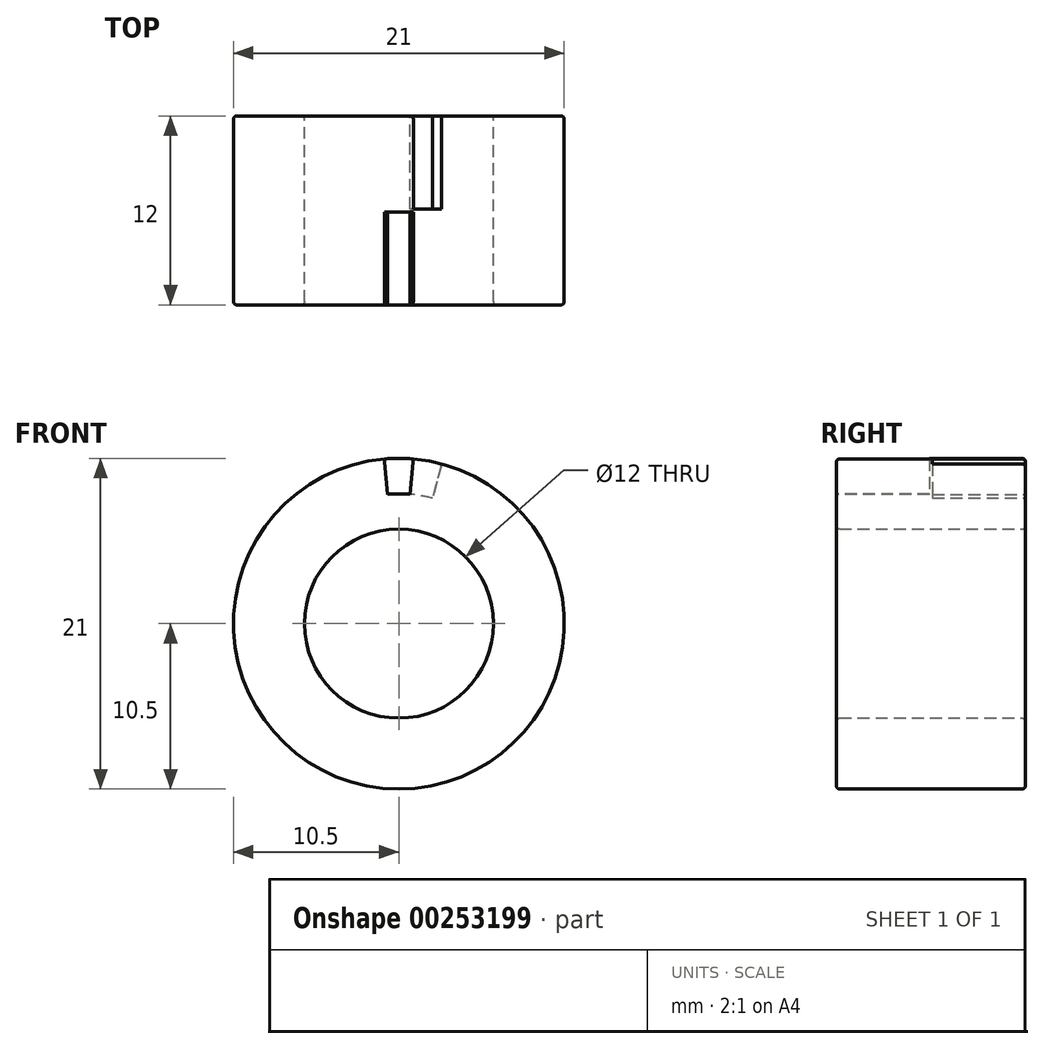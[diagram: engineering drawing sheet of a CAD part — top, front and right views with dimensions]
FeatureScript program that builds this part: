
annotation { "Feature Type Name" : "Feature", "Feature Type Description" : "" }
export const myFeature = defineFeature(function(context is Context, id is Id, definition is map)
    precondition{}
    {
        {
            var Q0;
            Q0=qCreatedBy(makeId("Front.planeOp"),FACE);
            var sketch = newSketch(context, id + "F0", { "sketchPlane" : qUnion([Q0])});
            skCircle(sketch, "E0", {"center": v(0, 0) * mm, "radius": 10.5 * mm});
            skCircle(sketch, "E1", {"center": v(0, 0) * mm, "radius": 6 * mm});
            skSolve(sketch);
        }
        {
            var Q0;
            Q0 = qSketchRegion(id + "F0", true);
            extrude(context, id + "F1", {"entities" : qUnion([Q0]), "depth" : 12 * mm});
        }
        {
            var Q0;
            Q0=makeQuery(id+"F1.opExtrude","CAP_FACE",FACE,{"disambiguationData":[OSD([sQuery(id+"F0.wireOp",EDGE,"E0"),sQuery(id+"F0.wireOp",EDGE,"E1")])],"isStart":false});
            var sketch = newSketch(context, id + "F2", { "sketchPlane" : qUnion([Q0])});
            skLineSegment(sketch, "E2", {"start": v(-0.92, 10.46) * mm, "end": v(-0.72, 8.22) * mm});
            skLineSegment(sketch, "E3", {"start": v(0.92, 10.46) * mm, "end": v(0.72, 8.22) * mm});
            skLineSegment(sketch, "E4", {"start": v(-0.92, 10.46) * mm, "end": v(-0.52, 5.98) * mm, "construction": true});
            skLineSegment(sketch, "E5", {"start": v(-0.52, 5.98) * mm, "end": v(0, 0) * mm, "construction": true});
            skLineSegment(sketch, "E6", {"start": v(0, 0) * mm, "end": v(0.52, 5.98) * mm, "construction": true});
            skLineSegment(sketch, "E7", {"start": v(0.52, 5.98) * mm, "end": v(0.92, 10.46) * mm, "construction": true});
            skPoint(sketch, "E8", {"position": v(-0.72, 8.22) * mm});
            skPoint(sketch, "E9", {"position": v(0.72, 8.22) * mm});
            skArc(sketch, "E10", {"start": v(0.72, 8.22) * mm, "mid": v(0, 8.25) * mm, "end": v(-0.72, 8.22) * mm});
            skArc(sketch, "E11.0", {"start": v(0.92, 10.46) * mm, "mid": v(0, 10.5) * mm, "end": v(-0.92, 10.46) * mm});
            skLineSegment(sketch, "E12", {"start": v(0, 0) * mm, "end": v(0, 8.25) * mm});
            skSolve(sketch);
        }
        {
            var Q0;
            Q0 = qSketchRegion(id + "F2", true);
            extrude(context, id + "F3", {"entities" : qUnion([Q0]), "operationType" : NewBodyOperationType.REMOVE, "oppositeDirection" : true, "depth" : 5.9 * mm});
        }
        {
            var Q0;
            Q0=makeQuery(id+"F1.opExtrude","CAP_FACE",FACE,{"disambiguationData":[OSD([sQuery(id+"F0.wireOp",EDGE,"E0"),sQuery(id+"F0.wireOp",EDGE,"E1")])],"isStart":true});
            var sketch = newSketch(context, id + "F4", { "sketchPlane" : qUnion([Q0])});
            skLineSegment(sketch, "E13", {"start": v(-2.72, 10.14) * mm, "end": v(-2.14, 7.97) * mm});
            skLineSegment(sketch, "E14", {"start": v(-0.92, 10.46) * mm, "end": v(-0.72, 8.22) * mm});
            skLineSegment(sketch, "E15", {"start": v(-2.72, 10.14) * mm, "end": v(-1.55, 5.8) * mm, "construction": true});
            skLineSegment(sketch, "E16", {"start": v(-1.55, 5.8) * mm, "end": v(0, 0) * mm, "construction": true});
            skLineSegment(sketch, "E17", {"start": v(0, 0) * mm, "end": v(-0.52, 5.98) * mm, "construction": true});
            skLineSegment(sketch, "E18", {"start": v(-0.52, 5.98) * mm, "end": v(-0.92, 10.46) * mm, "construction": true});
            skPoint(sketch, "E19", {"position": v(-2.14, 7.97) * mm});
            skPoint(sketch, "E20", {"position": v(-0.72, 8.22) * mm});
            skArc(sketch, "E21", {"start": v(-0.72, 8.22) * mm, "mid": v(-1.43, 8.12) * mm, "end": v(-2.14, 7.97) * mm});
            skArc(sketch, "E22.0", {"start": v(-0.92, 10.46) * mm, "mid": v(-1.82, 10.34) * mm, "end": v(-2.72, 10.14) * mm});
            skLineSegment(sketch, "E23", {"start": v(0, 0) * mm, "end": v(-1.43, 8.12) * mm});
            skSolve(sketch);
        }
        {
            var Q0;
            Q0 = qSketchRegion(id + "F4", true);
            extrude(context, id + "F5", {"entities" : qUnion([Q0]), "operationType" : NewBodyOperationType.REMOVE, "oppositeDirection" : true, "depth" : 5.9 * mm});
        }
        {
            var Q0;
            Q0=makeQuery(id+"F1.opExtrude","CAP_EDGE",EDGE,{"disambiguationData":[OSD([sQuery(id+"F0.wireOp",EDGE,"E1")])],"isStart":true});
            var Q1;
            {var subQ0=sQuery(id+"F0.wireOp",EDGE,"E0");var subQ3=sQuery(id+"F4.wireOp",EDGE,"E14");var subQ4=makeQuery(id+"FM8r0xqs9yAwbjn_1.16.F5.opExtrude","SWEPT_FACE",FACE,{"disambiguationData":[OSD([subQ3])]});var subQ5=sQuery(id+"F4.wireOp",EDGE,"E13");var subQ6=makeQuery(id+"F5.boolean.opBoolean","COPY",FACE,{"derivedFrom":makeQuery(id+"F5.opExtrude","SWEPT_FACE",FACE,{"disambiguationData":[OSD([subQ5])]})});Q1=makeQuery(id+"FM8r0xqs9yAwbjn_1.17.F5.boolean.opBoolean","SPLIT",EDGE,{"disambiguationData":[TD([makeQuery(id+"FM8r0xqs9yAwbjn_1.16.F5.boolean.opBoolean","COPY",FACE,{"derivedFrom":subQ4})])],"derivedFrom":makeQuery(id+"FM8r0xqs9yAwbjn_1.16.F5.boolean.opBoolean","SPLIT",EDGE,{"disambiguationData":[TD([subQ6])],"derivedFrom":makeQuery(id+"FM8r0xqs9yAwbjn_1.15.F5.boolean.opBoolean","SPLIT",EDGE,{"disambiguationData":[TD([subQ6])],"derivedFrom":makeQuery(id+"FM8r0xqs9yAwbjn_1.14.F5.boolean.opBoolean","SPLIT",EDGE,{"disambiguationData":[TD([subQ6])],"derivedFrom":makeQuery(id+"FM8r0xqs9yAwbjn_1.13.F5.boolean.opBoolean","SPLIT",EDGE,{"disambiguationData":[TD([subQ6])],"derivedFrom":makeQuery(id+"FM8r0xqs9yAwbjn_1.12.F5.boolean.opBoolean","SPLIT",EDGE,{"disambiguationData":[TD([subQ6])],"derivedFrom":makeQuery(id+"FM8r0xqs9yAwbjn_1.11.F5.boolean.opBoolean","SPLIT",EDGE,{"disambiguationData":[TD([subQ6])],"derivedFrom":makeQuery(id+"FM8r0xqs9yAwbjn_1.10.F5.boolean.opBoolean","SPLIT",EDGE,{"disambiguationData":[TD([subQ6])],"derivedFrom":makeQuery(id+"FM8r0xqs9yAwbjn_1.9.F5.boolean.opBoolean","SPLIT",EDGE,{"disambiguationData":[TD([subQ6])],"derivedFrom":makeQuery(id+"FM8r0xqs9yAwbjn_1.8.F5.boolean.opBoolean","SPLIT",EDGE,{"disambiguationData":[TD([subQ6])],"derivedFrom":makeQuery(id+"FM8r0xqs9yAwbjn_1.7.F5.boolean.opBoolean","SPLIT",EDGE,{"disambiguationData":[TD([subQ6])],"derivedFrom":makeQuery(id+"FM8r0xqs9yAwbjn_1.6.F5.boolean.opBoolean","SPLIT",EDGE,{"disambiguationData":[TD([subQ6])],"derivedFrom":makeQuery(id+"FM8r0xqs9yAwbjn_1.5.F5.boolean.opBoolean","SPLIT",EDGE,{"disambiguationData":[TD([subQ6])],"derivedFrom":makeQuery(id+"FM8r0xqs9yAwbjn_1.4.F5.boolean.opBoolean","SPLIT",EDGE,{"disambiguationData":[TD([subQ6])],"derivedFrom":makeQuery(id+"FM8r0xqs9yAwbjn_1.3.F5.boolean.opBoolean","SPLIT",EDGE,{"disambiguationData":[TD([subQ6])],"derivedFrom":makeQuery(id+"FM8r0xqs9yAwbjn_1.2.F5.boolean.opBoolean","SPLIT",EDGE,{"disambiguationData":[TD([subQ6])],"derivedFrom":makeQuery(id+"FM8r0xqs9yAwbjn_1.1.F5.boolean.opBoolean","SPLIT",EDGE,{"disambiguationData":[TD([subQ6])],"derivedFrom":makeQuery(id+"F1.opExtrude","CAP_EDGE",EDGE,{"disambiguationData":[OSD([subQ0])],"isStart":true})})})})})})})})})})})})})})})})})});}
            var Q2;
            {var subQ0=sQuery(id+"F0.wireOp",EDGE,"E0");var subQ3=sQuery(id+"F4.wireOp",EDGE,"E14");var subQ4=makeQuery(id+"FM8r0xqs9yAwbjn_1.15.F5.opExtrude","SWEPT_FACE",FACE,{"disambiguationData":[OSD([subQ3])]});var subQ5=sQuery(id+"F4.wireOp",EDGE,"E13");var subQ6=makeQuery(id+"F5.boolean.opBoolean","COPY",FACE,{"derivedFrom":makeQuery(id+"F5.opExtrude","SWEPT_FACE",FACE,{"disambiguationData":[OSD([subQ5])]})});Q2=makeQuery(id+"FM8r0xqs9yAwbjn_1.16.F5.boolean.opBoolean","SPLIT",EDGE,{"disambiguationData":[TD([makeQuery(id+"FM8r0xqs9yAwbjn_1.15.F5.boolean.opBoolean","COPY",FACE,{"derivedFrom":subQ4})])],"derivedFrom":makeQuery(id+"FM8r0xqs9yAwbjn_1.15.F5.boolean.opBoolean","SPLIT",EDGE,{"disambiguationData":[TD([subQ6])],"derivedFrom":makeQuery(id+"FM8r0xqs9yAwbjn_1.14.F5.boolean.opBoolean","SPLIT",EDGE,{"disambiguationData":[TD([subQ6])],"derivedFrom":makeQuery(id+"FM8r0xqs9yAwbjn_1.13.F5.boolean.opBoolean","SPLIT",EDGE,{"disambiguationData":[TD([subQ6])],"derivedFrom":makeQuery(id+"FM8r0xqs9yAwbjn_1.12.F5.boolean.opBoolean","SPLIT",EDGE,{"disambiguationData":[TD([subQ6])],"derivedFrom":makeQuery(id+"FM8r0xqs9yAwbjn_1.11.F5.boolean.opBoolean","SPLIT",EDGE,{"disambiguationData":[TD([subQ6])],"derivedFrom":makeQuery(id+"FM8r0xqs9yAwbjn_1.10.F5.boolean.opBoolean","SPLIT",EDGE,{"disambiguationData":[TD([subQ6])],"derivedFrom":makeQuery(id+"FM8r0xqs9yAwbjn_1.9.F5.boolean.opBoolean","SPLIT",EDGE,{"disambiguationData":[TD([subQ6])],"derivedFrom":makeQuery(id+"FM8r0xqs9yAwbjn_1.8.F5.boolean.opBoolean","SPLIT",EDGE,{"disambiguationData":[TD([subQ6])],"derivedFrom":makeQuery(id+"FM8r0xqs9yAwbjn_1.7.F5.boolean.opBoolean","SPLIT",EDGE,{"disambiguationData":[TD([subQ6])],"derivedFrom":makeQuery(id+"FM8r0xqs9yAwbjn_1.6.F5.boolean.opBoolean","SPLIT",EDGE,{"disambiguationData":[TD([subQ6])],"derivedFrom":makeQuery(id+"FM8r0xqs9yAwbjn_1.5.F5.boolean.opBoolean","SPLIT",EDGE,{"disambiguationData":[TD([subQ6])],"derivedFrom":makeQuery(id+"FM8r0xqs9yAwbjn_1.4.F5.boolean.opBoolean","SPLIT",EDGE,{"disambiguationData":[TD([subQ6])],"derivedFrom":makeQuery(id+"FM8r0xqs9yAwbjn_1.3.F5.boolean.opBoolean","SPLIT",EDGE,{"disambiguationData":[TD([subQ6])],"derivedFrom":makeQuery(id+"FM8r0xqs9yAwbjn_1.2.F5.boolean.opBoolean","SPLIT",EDGE,{"disambiguationData":[TD([subQ6])],"derivedFrom":makeQuery(id+"FM8r0xqs9yAwbjn_1.1.F5.boolean.opBoolean","SPLIT",EDGE,{"disambiguationData":[TD([subQ6])],"derivedFrom":makeQuery(id+"F1.opExtrude","CAP_EDGE",EDGE,{"disambiguationData":[OSD([subQ0])],"isStart":true})})})})})})})})})})})})})})})})});}
            var Q3;
            Q3=makeQuery(id+"FM8r0xqs9yAwbjn_1.16.F5.boolean.opBoolean","COPY",EDGE,{"derivedFrom":makeQuery(id+"FM8r0xqs9yAwbjn_1.16.F5.opExtrude","CAP_EDGE",EDGE,{"disambiguationData":[OSD([sQuery(id+"F4.wireOp",EDGE,"E21")])],"isStart":true})});
            var Q4;
            Q4=makeQuery(id+"FM8r0xqs9yAwbjn_1.16.F5.boolean.opBoolean","COPY",EDGE,{"derivedFrom":makeQuery(id+"FM8r0xqs9yAwbjn_1.16.F5.opExtrude","CAP_EDGE",EDGE,{"disambiguationData":[OSD([sQuery(id+"F4.wireOp",EDGE,"E14")])],"isStart":true})});
            var Q5;
            Q5=makeQuery(id+"FM8r0xqs9yAwbjn_1.16.F5.boolean.opBoolean","COPY",EDGE,{"derivedFrom":makeQuery(id+"FM8r0xqs9yAwbjn_1.16.F5.opExtrude","CAP_EDGE",EDGE,{"disambiguationData":[OSD([sQuery(id+"F4.wireOp",EDGE,"E13")])],"isStart":true})});
            var Q6;
            Q6=makeQuery(id+"FM8r0xqs9yAwbjn_1.16.F5.boolean.opBoolean","COPY",EDGE,{"derivedFrom":makeQuery(id+"FM8r0xqs9yAwbjn_1.16.F5.opExtrude","SWEPT_EDGE",EDGE,{"disambiguationData":[OSD([sQuery(id+"F0.wireOp",EDGE,"E0"),sQuery(id+"F4.wireOp",EDGE,"E13"),sQuery(id+"F4.wireOp",EDGE,"E22.0")])]})});
            var Q7;
            Q7=makeQuery(id+"FM8r0xqs9yAwbjn_1.16.F5.boolean.opBoolean","COPY",EDGE,{"derivedFrom":makeQuery(id+"FM8r0xqs9yAwbjn_1.16.F5.opExtrude","SWEPT_EDGE",EDGE,{"disambiguationData":[OSD([sQuery(id+"F0.wireOp",EDGE,"E0"),sQuery(id+"F4.wireOp",EDGE,"E14"),sQuery(id+"F4.wireOp",EDGE,"E22.0")])]})});
            var Q8;
            Q8=makeQuery(id+"FM8r0xqs9yAwbjn_1.17.F5.boolean.opBoolean","COPY",EDGE,{"derivedFrom":makeQuery(id+"FM8r0xqs9yAwbjn_1.17.F5.opExtrude","SWEPT_EDGE",EDGE,{"disambiguationData":[OSD([sQuery(id+"F0.wireOp",EDGE,"E0"),sQuery(id+"F4.wireOp",EDGE,"E13"),sQuery(id+"F4.wireOp",EDGE,"E22.0")])]})});
            var Q9;
            Q9=makeQuery(id+"FM8r0xqs9yAwbjn_1.17.F5.boolean.opBoolean","COPY",EDGE,{"derivedFrom":makeQuery(id+"FM8r0xqs9yAwbjn_1.17.F5.opExtrude","CAP_EDGE",EDGE,{"disambiguationData":[OSD([sQuery(id+"F4.wireOp",EDGE,"E13")])],"isStart":true})});
            var Q10;
            Q10=makeQuery(id+"FM8r0xqs9yAwbjn_1.17.F5.boolean.opBoolean","COPY",EDGE,{"derivedFrom":makeQuery(id+"FM8r0xqs9yAwbjn_1.17.F5.opExtrude","CAP_EDGE",EDGE,{"disambiguationData":[OSD([sQuery(id+"F4.wireOp",EDGE,"E21")])],"isStart":true})});
            var Q11;
            Q11=makeQuery(id+"FM8r0xqs9yAwbjn_1.17.F5.boolean.opBoolean","COPY",EDGE,{"derivedFrom":makeQuery(id+"FM8r0xqs9yAwbjn_1.17.F5.opExtrude","SWEPT_EDGE",EDGE,{"disambiguationData":[OSD([sQuery(id+"F0.wireOp",EDGE,"E0"),sQuery(id+"F4.wireOp",EDGE,"E14"),sQuery(id+"F4.wireOp",EDGE,"E22.0")])]})});
            var Q12;
            Q12=makeQuery(id+"FM8r0xqs9yAwbjn_1.17.F5.boolean.opBoolean","COPY",EDGE,{"derivedFrom":makeQuery(id+"FM8r0xqs9yAwbjn_1.17.F5.opExtrude","CAP_EDGE",EDGE,{"disambiguationData":[OSD([sQuery(id+"F4.wireOp",EDGE,"E14")])],"isStart":true})});
            var Q13;
            Q13=makeQuery(id+"F5.boolean.opBoolean","COPY",EDGE,{"derivedFrom":makeQuery(id+"F5.opExtrude","SWEPT_EDGE",EDGE,{"disambiguationData":[OSD([sQuery(id+"F0.wireOp",EDGE,"E0"),sQuery(id+"F4.wireOp",EDGE,"E13"),sQuery(id+"F4.wireOp",EDGE,"E22.0")])]})});
            var Q14;
            {var subQ0=sQuery(id+"F0.wireOp",EDGE,"E0");var subQ3=makeQuery(id+"F5.boolean.opBoolean","COPY",FACE,{"derivedFrom":makeQuery(id+"F5.opExtrude","SWEPT_FACE",FACE,{"disambiguationData":[OSD([sQuery(id+"F4.wireOp",EDGE,"E13")])]})});Q14=makeQuery(id+"FM8r0xqs9yAwbjn_1.17.F5.boolean.opBoolean","SPLIT",EDGE,{"disambiguationData":[TD([subQ3])],"derivedFrom":makeQuery(id+"FM8r0xqs9yAwbjn_1.16.F5.boolean.opBoolean","SPLIT",EDGE,{"disambiguationData":[TD([subQ3])],"derivedFrom":makeQuery(id+"FM8r0xqs9yAwbjn_1.15.F5.boolean.opBoolean","SPLIT",EDGE,{"disambiguationData":[TD([subQ3])],"derivedFrom":makeQuery(id+"FM8r0xqs9yAwbjn_1.14.F5.boolean.opBoolean","SPLIT",EDGE,{"disambiguationData":[TD([subQ3])],"derivedFrom":makeQuery(id+"FM8r0xqs9yAwbjn_1.13.F5.boolean.opBoolean","SPLIT",EDGE,{"disambiguationData":[TD([subQ3])],"derivedFrom":makeQuery(id+"FM8r0xqs9yAwbjn_1.12.F5.boolean.opBoolean","SPLIT",EDGE,{"disambiguationData":[TD([subQ3])],"derivedFrom":makeQuery(id+"FM8r0xqs9yAwbjn_1.11.F5.boolean.opBoolean","SPLIT",EDGE,{"disambiguationData":[TD([subQ3])],"derivedFrom":makeQuery(id+"FM8r0xqs9yAwbjn_1.10.F5.boolean.opBoolean","SPLIT",EDGE,{"disambiguationData":[TD([subQ3])],"derivedFrom":makeQuery(id+"FM8r0xqs9yAwbjn_1.9.F5.boolean.opBoolean","SPLIT",EDGE,{"disambiguationData":[TD([subQ3])],"derivedFrom":makeQuery(id+"FM8r0xqs9yAwbjn_1.8.F5.boolean.opBoolean","SPLIT",EDGE,{"disambiguationData":[TD([subQ3])],"derivedFrom":makeQuery(id+"FM8r0xqs9yAwbjn_1.7.F5.boolean.opBoolean","SPLIT",EDGE,{"disambiguationData":[TD([subQ3])],"derivedFrom":makeQuery(id+"FM8r0xqs9yAwbjn_1.6.F5.boolean.opBoolean","SPLIT",EDGE,{"disambiguationData":[TD([subQ3])],"derivedFrom":makeQuery(id+"FM8r0xqs9yAwbjn_1.5.F5.boolean.opBoolean","SPLIT",EDGE,{"disambiguationData":[TD([subQ3])],"derivedFrom":makeQuery(id+"FM8r0xqs9yAwbjn_1.4.F5.boolean.opBoolean","SPLIT",EDGE,{"disambiguationData":[TD([subQ3])],"derivedFrom":makeQuery(id+"FM8r0xqs9yAwbjn_1.3.F5.boolean.opBoolean","SPLIT",EDGE,{"disambiguationData":[TD([subQ3])],"derivedFrom":makeQuery(id+"FM8r0xqs9yAwbjn_1.2.F5.boolean.opBoolean","SPLIT",EDGE,{"disambiguationData":[TD([subQ3])],"derivedFrom":makeQuery(id+"FM8r0xqs9yAwbjn_1.1.F5.boolean.opBoolean","SPLIT",EDGE,{"disambiguationData":[TD([subQ3])],"derivedFrom":makeQuery(id+"F1.opExtrude","CAP_EDGE",EDGE,{"disambiguationData":[OSD([subQ0])],"isStart":true})})})})})})})})})})})})})})})})})});}
            var Q15;
            Q15=makeQuery(id+"F5.boolean.opBoolean","COPY",EDGE,{"derivedFrom":makeQuery(id+"F5.opExtrude","CAP_EDGE",EDGE,{"disambiguationData":[OSD([sQuery(id+"F4.wireOp",EDGE,"E13")])],"isStart":true})});
            var Q16;
            Q16=makeQuery(id+"F5.boolean.opBoolean","COPY",EDGE,{"derivedFrom":makeQuery(id+"F5.opExtrude","CAP_EDGE",EDGE,{"disambiguationData":[OSD([sQuery(id+"F4.wireOp",EDGE,"E21")])],"isStart":true})});
            var Q17;
            Q17=makeQuery(id+"F5.boolean.opBoolean","COPY",EDGE,{"derivedFrom":makeQuery(id+"F5.opExtrude","SWEPT_EDGE",EDGE,{"disambiguationData":[OSD([sQuery(id+"F0.wireOp",EDGE,"E0"),sQuery(id+"F4.wireOp",EDGE,"E14"),sQuery(id+"F4.wireOp",EDGE,"E22.0")])]})});
            var Q18;
            Q18=makeQuery(id+"F5.boolean.opBoolean","COPY",EDGE,{"derivedFrom":makeQuery(id+"F5.opExtrude","CAP_EDGE",EDGE,{"disambiguationData":[OSD([sQuery(id+"F4.wireOp",EDGE,"E14")])],"isStart":true})});
            var Q19;
            Q19=makeQuery(id+"FM8r0xqs9yAwbjn_1.1.F5.boolean.opBoolean","COPY",EDGE,{"derivedFrom":makeQuery(id+"FM8r0xqs9yAwbjn_1.1.F5.opExtrude","CAP_EDGE",EDGE,{"disambiguationData":[OSD([sQuery(id+"F4.wireOp",EDGE,"E13")])],"isStart":true})});
            var Q20;
            Q20=makeQuery(id+"FM8r0xqs9yAwbjn_1.1.F5.boolean.opBoolean","COPY",EDGE,{"derivedFrom":makeQuery(id+"FM8r0xqs9yAwbjn_1.1.F5.opExtrude","SWEPT_EDGE",EDGE,{"disambiguationData":[OSD([sQuery(id+"F0.wireOp",EDGE,"E0"),sQuery(id+"F4.wireOp",EDGE,"E13"),sQuery(id+"F4.wireOp",EDGE,"E22.0")])]})});
            var Q21;
            Q21=makeQuery(id+"FM8r0xqs9yAwbjn_1.1.F5.boolean.opBoolean","COPY",EDGE,{"derivedFrom":makeQuery(id+"FM8r0xqs9yAwbjn_1.1.F5.opExtrude","SWEPT_EDGE",EDGE,{"disambiguationData":[OSD([sQuery(id+"F0.wireOp",EDGE,"E0"),sQuery(id+"F4.wireOp",EDGE,"E14"),sQuery(id+"F4.wireOp",EDGE,"E22.0")])]})});
            var Q22;
            Q22=makeQuery(id+"FM8r0xqs9yAwbjn_1.1.F5.boolean.opBoolean","COPY",EDGE,{"derivedFrom":makeQuery(id+"FM8r0xqs9yAwbjn_1.1.F5.opExtrude","CAP_EDGE",EDGE,{"disambiguationData":[OSD([sQuery(id+"F4.wireOp",EDGE,"E14")])],"isStart":true})});
            var Q23;
            Q23=makeQuery(id+"FM8r0xqs9yAwbjn_1.1.F5.boolean.opBoolean","COPY",EDGE,{"derivedFrom":makeQuery(id+"FM8r0xqs9yAwbjn_1.1.F5.opExtrude","CAP_EDGE",EDGE,{"disambiguationData":[OSD([sQuery(id+"F4.wireOp",EDGE,"E21")])],"isStart":true})});
            var Q24;
            {var subQ0=sQuery(id+"F0.wireOp",EDGE,"E0");var subQ3=makeQuery(id+"FM8r0xqs9yAwbjn_1.1.F5.opExtrude","SWEPT_FACE",FACE,{"disambiguationData":[OSD([sQuery(id+"F4.wireOp",EDGE,"E14")])]});var subQ4=sQuery(id+"F4.wireOp",EDGE,"E13");Q24=makeQuery(id+"FM8r0xqs9yAwbjn_1.2.F5.boolean.opBoolean","SPLIT",EDGE,{"disambiguationData":[TD([makeQuery(id+"FM8r0xqs9yAwbjn_1.1.F5.boolean.opBoolean","COPY",FACE,{"derivedFrom":subQ3})])],"derivedFrom":makeQuery(id+"FM8r0xqs9yAwbjn_1.1.F5.boolean.opBoolean","SPLIT",EDGE,{"disambiguationData":[TD([makeQuery(id+"F5.boolean.opBoolean","COPY",FACE,{"derivedFrom":makeQuery(id+"F5.opExtrude","SWEPT_FACE",FACE,{"disambiguationData":[OSD([subQ4])]})})])],"derivedFrom":makeQuery(id+"F1.opExtrude","CAP_EDGE",EDGE,{"disambiguationData":[OSD([subQ0])],"isStart":true})})});}
            var Q25;
            Q25=makeQuery(id+"FM8r0xqs9yAwbjn_1.2.F5.boolean.opBoolean","COPY",EDGE,{"derivedFrom":makeQuery(id+"FM8r0xqs9yAwbjn_1.2.F5.opExtrude","CAP_EDGE",EDGE,{"disambiguationData":[OSD([sQuery(id+"F4.wireOp",EDGE,"E13")])],"isStart":true})});
            var Q26;
            Q26=makeQuery(id+"FM8r0xqs9yAwbjn_1.2.F5.boolean.opBoolean","COPY",EDGE,{"derivedFrom":makeQuery(id+"FM8r0xqs9yAwbjn_1.2.F5.opExtrude","SWEPT_EDGE",EDGE,{"disambiguationData":[OSD([sQuery(id+"F0.wireOp",EDGE,"E0"),sQuery(id+"F4.wireOp",EDGE,"E13"),sQuery(id+"F4.wireOp",EDGE,"E22.0")])]})});
            var Q27;
            Q27=makeQuery(id+"FM8r0xqs9yAwbjn_1.2.F5.boolean.opBoolean","COPY",EDGE,{"derivedFrom":makeQuery(id+"FM8r0xqs9yAwbjn_1.2.F5.opExtrude","SWEPT_EDGE",EDGE,{"disambiguationData":[OSD([sQuery(id+"F0.wireOp",EDGE,"E0"),sQuery(id+"F4.wireOp",EDGE,"E14"),sQuery(id+"F4.wireOp",EDGE,"E22.0")])]})});
            var Q28;
            Q28=makeQuery(id+"FM8r0xqs9yAwbjn_1.2.F5.boolean.opBoolean","COPY",EDGE,{"derivedFrom":makeQuery(id+"FM8r0xqs9yAwbjn_1.2.F5.opExtrude","CAP_EDGE",EDGE,{"disambiguationData":[OSD([sQuery(id+"F4.wireOp",EDGE,"E21")])],"isStart":true})});
            var Q29;
            Q29=makeQuery(id+"FM8r0xqs9yAwbjn_1.2.F5.boolean.opBoolean","COPY",EDGE,{"derivedFrom":makeQuery(id+"FM8r0xqs9yAwbjn_1.2.F5.opExtrude","CAP_EDGE",EDGE,{"disambiguationData":[OSD([sQuery(id+"F4.wireOp",EDGE,"E14")])],"isStart":true})});
            var Q30;
            {var subQ0=sQuery(id+"F0.wireOp",EDGE,"E0");var subQ3=sQuery(id+"F4.wireOp",EDGE,"E14");var subQ4=makeQuery(id+"FM8r0xqs9yAwbjn_1.2.F5.opExtrude","SWEPT_FACE",FACE,{"disambiguationData":[OSD([subQ3])]});var subQ5=sQuery(id+"F4.wireOp",EDGE,"E13");var subQ6=makeQuery(id+"F5.boolean.opBoolean","COPY",FACE,{"derivedFrom":makeQuery(id+"F5.opExtrude","SWEPT_FACE",FACE,{"disambiguationData":[OSD([subQ5])]})});Q30=makeQuery(id+"FM8r0xqs9yAwbjn_1.3.F5.boolean.opBoolean","SPLIT",EDGE,{"disambiguationData":[TD([makeQuery(id+"FM8r0xqs9yAwbjn_1.2.F5.boolean.opBoolean","COPY",FACE,{"derivedFrom":subQ4})])],"derivedFrom":makeQuery(id+"FM8r0xqs9yAwbjn_1.2.F5.boolean.opBoolean","SPLIT",EDGE,{"disambiguationData":[TD([subQ6])],"derivedFrom":makeQuery(id+"FM8r0xqs9yAwbjn_1.1.F5.boolean.opBoolean","SPLIT",EDGE,{"disambiguationData":[TD([subQ6])],"derivedFrom":makeQuery(id+"F1.opExtrude","CAP_EDGE",EDGE,{"disambiguationData":[OSD([subQ0])],"isStart":true})})})});}
            var Q31;
            Q31=makeQuery(id+"FM8r0xqs9yAwbjn_1.3.F5.boolean.opBoolean","COPY",EDGE,{"derivedFrom":makeQuery(id+"FM8r0xqs9yAwbjn_1.3.F5.opExtrude","CAP_EDGE",EDGE,{"disambiguationData":[OSD([sQuery(id+"F4.wireOp",EDGE,"E13")])],"isStart":true})});
            var Q32;
            Q32=makeQuery(id+"FM8r0xqs9yAwbjn_1.3.F5.boolean.opBoolean","COPY",EDGE,{"derivedFrom":makeQuery(id+"FM8r0xqs9yAwbjn_1.3.F5.opExtrude","SWEPT_EDGE",EDGE,{"disambiguationData":[OSD([sQuery(id+"F0.wireOp",EDGE,"E0"),sQuery(id+"F4.wireOp",EDGE,"E13"),sQuery(id+"F4.wireOp",EDGE,"E22.0")])]})});
            var Q33;
            Q33=makeQuery(id+"FM8r0xqs9yAwbjn_1.3.F5.boolean.opBoolean","COPY",EDGE,{"derivedFrom":makeQuery(id+"FM8r0xqs9yAwbjn_1.3.F5.opExtrude","SWEPT_EDGE",EDGE,{"disambiguationData":[OSD([sQuery(id+"F0.wireOp",EDGE,"E0"),sQuery(id+"F4.wireOp",EDGE,"E14"),sQuery(id+"F4.wireOp",EDGE,"E22.0")])]})});
            var Q34;
            Q34=makeQuery(id+"FM8r0xqs9yAwbjn_1.3.F5.boolean.opBoolean","COPY",EDGE,{"derivedFrom":makeQuery(id+"FM8r0xqs9yAwbjn_1.3.F5.opExtrude","CAP_EDGE",EDGE,{"disambiguationData":[OSD([sQuery(id+"F4.wireOp",EDGE,"E21")])],"isStart":true})});
            var Q35;
            {var subQ0=sQuery(id+"F0.wireOp",EDGE,"E0");var subQ3=sQuery(id+"F4.wireOp",EDGE,"E14");var subQ4=makeQuery(id+"FM8r0xqs9yAwbjn_1.3.F5.opExtrude","SWEPT_FACE",FACE,{"disambiguationData":[OSD([subQ3])]});var subQ5=sQuery(id+"F4.wireOp",EDGE,"E13");var subQ6=makeQuery(id+"F5.boolean.opBoolean","COPY",FACE,{"derivedFrom":makeQuery(id+"F5.opExtrude","SWEPT_FACE",FACE,{"disambiguationData":[OSD([subQ5])]})});Q35=makeQuery(id+"FM8r0xqs9yAwbjn_1.4.F5.boolean.opBoolean","SPLIT",EDGE,{"disambiguationData":[TD([makeQuery(id+"FM8r0xqs9yAwbjn_1.3.F5.boolean.opBoolean","COPY",FACE,{"derivedFrom":subQ4})])],"derivedFrom":makeQuery(id+"FM8r0xqs9yAwbjn_1.3.F5.boolean.opBoolean","SPLIT",EDGE,{"disambiguationData":[TD([subQ6])],"derivedFrom":makeQuery(id+"FM8r0xqs9yAwbjn_1.2.F5.boolean.opBoolean","SPLIT",EDGE,{"disambiguationData":[TD([subQ6])],"derivedFrom":makeQuery(id+"FM8r0xqs9yAwbjn_1.1.F5.boolean.opBoolean","SPLIT",EDGE,{"disambiguationData":[TD([subQ6])],"derivedFrom":makeQuery(id+"F1.opExtrude","CAP_EDGE",EDGE,{"disambiguationData":[OSD([subQ0])],"isStart":true})})})})});}
            var Q36;
            Q36=makeQuery(id+"FM8r0xqs9yAwbjn_1.4.F5.boolean.opBoolean","COPY",EDGE,{"derivedFrom":makeQuery(id+"FM8r0xqs9yAwbjn_1.4.F5.opExtrude","CAP_EDGE",EDGE,{"disambiguationData":[OSD([sQuery(id+"F4.wireOp",EDGE,"E13")])],"isStart":true})});
            var Q37;
            Q37=makeQuery(id+"FM8r0xqs9yAwbjn_1.4.F5.boolean.opBoolean","COPY",EDGE,{"derivedFrom":makeQuery(id+"FM8r0xqs9yAwbjn_1.4.F5.opExtrude","SWEPT_EDGE",EDGE,{"disambiguationData":[OSD([sQuery(id+"F0.wireOp",EDGE,"E0"),sQuery(id+"F4.wireOp",EDGE,"E13"),sQuery(id+"F4.wireOp",EDGE,"E22.0")])]})});
            var Q38;
            Q38=makeQuery(id+"FM8r0xqs9yAwbjn_1.4.F5.boolean.opBoolean","COPY",EDGE,{"derivedFrom":makeQuery(id+"FM8r0xqs9yAwbjn_1.4.F5.opExtrude","SWEPT_EDGE",EDGE,{"disambiguationData":[OSD([sQuery(id+"F0.wireOp",EDGE,"E0"),sQuery(id+"F4.wireOp",EDGE,"E14"),sQuery(id+"F4.wireOp",EDGE,"E22.0")])]})});
            var Q39;
            Q39=makeQuery(id+"FM8r0xqs9yAwbjn_1.4.F5.boolean.opBoolean","COPY",EDGE,{"derivedFrom":makeQuery(id+"FM8r0xqs9yAwbjn_1.4.F5.opExtrude","CAP_EDGE",EDGE,{"disambiguationData":[OSD([sQuery(id+"F4.wireOp",EDGE,"E21")])],"isStart":true})});
            var Q40;
            Q40=makeQuery(id+"FM8r0xqs9yAwbjn_1.4.F5.boolean.opBoolean","COPY",EDGE,{"derivedFrom":makeQuery(id+"FM8r0xqs9yAwbjn_1.4.F5.opExtrude","CAP_EDGE",EDGE,{"disambiguationData":[OSD([sQuery(id+"F4.wireOp",EDGE,"E14")])],"isStart":true})});
            var Q41;
            {var subQ0=sQuery(id+"F0.wireOp",EDGE,"E0");var subQ3=sQuery(id+"F4.wireOp",EDGE,"E14");var subQ4=makeQuery(id+"FM8r0xqs9yAwbjn_1.4.F5.opExtrude","SWEPT_FACE",FACE,{"disambiguationData":[OSD([subQ3])]});var subQ5=sQuery(id+"F4.wireOp",EDGE,"E13");var subQ6=makeQuery(id+"F5.boolean.opBoolean","COPY",FACE,{"derivedFrom":makeQuery(id+"F5.opExtrude","SWEPT_FACE",FACE,{"disambiguationData":[OSD([subQ5])]})});Q41=makeQuery(id+"FM8r0xqs9yAwbjn_1.5.F5.boolean.opBoolean","SPLIT",EDGE,{"disambiguationData":[TD([makeQuery(id+"FM8r0xqs9yAwbjn_1.4.F5.boolean.opBoolean","COPY",FACE,{"derivedFrom":subQ4})])],"derivedFrom":makeQuery(id+"FM8r0xqs9yAwbjn_1.4.F5.boolean.opBoolean","SPLIT",EDGE,{"disambiguationData":[TD([subQ6])],"derivedFrom":makeQuery(id+"FM8r0xqs9yAwbjn_1.3.F5.boolean.opBoolean","SPLIT",EDGE,{"disambiguationData":[TD([subQ6])],"derivedFrom":makeQuery(id+"FM8r0xqs9yAwbjn_1.2.F5.boolean.opBoolean","SPLIT",EDGE,{"disambiguationData":[TD([subQ6])],"derivedFrom":makeQuery(id+"FM8r0xqs9yAwbjn_1.1.F5.boolean.opBoolean","SPLIT",EDGE,{"disambiguationData":[TD([subQ6])],"derivedFrom":makeQuery(id+"F1.opExtrude","CAP_EDGE",EDGE,{"disambiguationData":[OSD([subQ0])],"isStart":true})})})})})});}
            var Q42;
            Q42=makeQuery(id+"FM8r0xqs9yAwbjn_1.5.F5.boolean.opBoolean","COPY",EDGE,{"derivedFrom":makeQuery(id+"FM8r0xqs9yAwbjn_1.5.F5.opExtrude","CAP_EDGE",EDGE,{"disambiguationData":[OSD([sQuery(id+"F4.wireOp",EDGE,"E13")])],"isStart":true})});
            var Q43;
            Q43=makeQuery(id+"FM8r0xqs9yAwbjn_1.5.F5.boolean.opBoolean","COPY",EDGE,{"derivedFrom":makeQuery(id+"FM8r0xqs9yAwbjn_1.5.F5.opExtrude","CAP_EDGE",EDGE,{"disambiguationData":[OSD([sQuery(id+"F4.wireOp",EDGE,"E21")])],"isStart":true})});
            var Q44;
            Q44=makeQuery(id+"FM8r0xqs9yAwbjn_1.5.F5.boolean.opBoolean","COPY",EDGE,{"derivedFrom":makeQuery(id+"FM8r0xqs9yAwbjn_1.5.F5.opExtrude","CAP_EDGE",EDGE,{"disambiguationData":[OSD([sQuery(id+"F4.wireOp",EDGE,"E14")])],"isStart":true})});
            var Q45;
            Q45=makeQuery(id+"FM8r0xqs9yAwbjn_1.5.F5.boolean.opBoolean","COPY",EDGE,{"derivedFrom":makeQuery(id+"FM8r0xqs9yAwbjn_1.5.F5.opExtrude","SWEPT_EDGE",EDGE,{"disambiguationData":[OSD([sQuery(id+"F0.wireOp",EDGE,"E0"),sQuery(id+"F4.wireOp",EDGE,"E13"),sQuery(id+"F4.wireOp",EDGE,"E22.0")])]})});
            var Q46;
            Q46=makeQuery(id+"FM8r0xqs9yAwbjn_1.5.F5.boolean.opBoolean","COPY",EDGE,{"derivedFrom":makeQuery(id+"FM8r0xqs9yAwbjn_1.5.F5.opExtrude","SWEPT_EDGE",EDGE,{"disambiguationData":[OSD([sQuery(id+"F0.wireOp",EDGE,"E0"),sQuery(id+"F4.wireOp",EDGE,"E14"),sQuery(id+"F4.wireOp",EDGE,"E22.0")])]})});
            var Q47;
            Q47=makeQuery(id+"FM8r0xqs9yAwbjn_1.6.F5.boolean.opBoolean","COPY",EDGE,{"derivedFrom":makeQuery(id+"FM8r0xqs9yAwbjn_1.6.F5.opExtrude","SWEPT_EDGE",EDGE,{"disambiguationData":[OSD([sQuery(id+"F0.wireOp",EDGE,"E0"),sQuery(id+"F4.wireOp",EDGE,"E13"),sQuery(id+"F4.wireOp",EDGE,"E22.0")])]})});
            var Q48;
            Q48=makeQuery(id+"FM8r0xqs9yAwbjn_1.6.F5.boolean.opBoolean","COPY",EDGE,{"derivedFrom":makeQuery(id+"FM8r0xqs9yAwbjn_1.6.F5.opExtrude","SWEPT_EDGE",EDGE,{"disambiguationData":[OSD([sQuery(id+"F0.wireOp",EDGE,"E0"),sQuery(id+"F4.wireOp",EDGE,"E14"),sQuery(id+"F4.wireOp",EDGE,"E22.0")])]})});
            var Q49;
            Q49=makeQuery(id+"FM8r0xqs9yAwbjn_1.6.F5.boolean.opBoolean","COPY",EDGE,{"derivedFrom":makeQuery(id+"FM8r0xqs9yAwbjn_1.6.F5.opExtrude","CAP_EDGE",EDGE,{"disambiguationData":[OSD([sQuery(id+"F4.wireOp",EDGE,"E13")])],"isStart":true})});
            var Q50;
            {var subQ0=sQuery(id+"F0.wireOp",EDGE,"E0");var subQ3=sQuery(id+"F4.wireOp",EDGE,"E14");var subQ4=makeQuery(id+"FM8r0xqs9yAwbjn_1.5.F5.opExtrude","SWEPT_FACE",FACE,{"disambiguationData":[OSD([subQ3])]});var subQ5=sQuery(id+"F4.wireOp",EDGE,"E13");var subQ6=makeQuery(id+"F5.boolean.opBoolean","COPY",FACE,{"derivedFrom":makeQuery(id+"F5.opExtrude","SWEPT_FACE",FACE,{"disambiguationData":[OSD([subQ5])]})});Q50=makeQuery(id+"FM8r0xqs9yAwbjn_1.6.F5.boolean.opBoolean","SPLIT",EDGE,{"disambiguationData":[TD([makeQuery(id+"FM8r0xqs9yAwbjn_1.5.F5.boolean.opBoolean","COPY",FACE,{"derivedFrom":subQ4})])],"derivedFrom":makeQuery(id+"FM8r0xqs9yAwbjn_1.5.F5.boolean.opBoolean","SPLIT",EDGE,{"disambiguationData":[TD([subQ6])],"derivedFrom":makeQuery(id+"FM8r0xqs9yAwbjn_1.4.F5.boolean.opBoolean","SPLIT",EDGE,{"disambiguationData":[TD([subQ6])],"derivedFrom":makeQuery(id+"FM8r0xqs9yAwbjn_1.3.F5.boolean.opBoolean","SPLIT",EDGE,{"disambiguationData":[TD([subQ6])],"derivedFrom":makeQuery(id+"FM8r0xqs9yAwbjn_1.2.F5.boolean.opBoolean","SPLIT",EDGE,{"disambiguationData":[TD([subQ6])],"derivedFrom":makeQuery(id+"FM8r0xqs9yAwbjn_1.1.F5.boolean.opBoolean","SPLIT",EDGE,{"disambiguationData":[TD([subQ6])],"derivedFrom":makeQuery(id+"F1.opExtrude","CAP_EDGE",EDGE,{"disambiguationData":[OSD([subQ0])],"isStart":true})})})})})})});}
            var Q51;
            Q51=makeQuery(id+"FM8r0xqs9yAwbjn_1.6.F5.boolean.opBoolean","COPY",EDGE,{"derivedFrom":makeQuery(id+"FM8r0xqs9yAwbjn_1.6.F5.opExtrude","CAP_EDGE",EDGE,{"disambiguationData":[OSD([sQuery(id+"F4.wireOp",EDGE,"E21")])],"isStart":true})});
            var Q52;
            Q52=makeQuery(id+"FM8r0xqs9yAwbjn_1.6.F5.boolean.opBoolean","COPY",EDGE,{"derivedFrom":makeQuery(id+"FM8r0xqs9yAwbjn_1.6.F5.opExtrude","CAP_EDGE",EDGE,{"disambiguationData":[OSD([sQuery(id+"F4.wireOp",EDGE,"E14")])],"isStart":true})});
            var Q53;
            Q53=makeQuery(id+"FM8r0xqs9yAwbjn_1.7.F5.boolean.opBoolean","COPY",EDGE,{"derivedFrom":makeQuery(id+"FM8r0xqs9yAwbjn_1.7.F5.opExtrude","CAP_EDGE",EDGE,{"disambiguationData":[OSD([sQuery(id+"F4.wireOp",EDGE,"E13")])],"isStart":true})});
            var Q54;
            Q54=makeQuery(id+"FM8r0xqs9yAwbjn_1.7.F5.boolean.opBoolean","COPY",EDGE,{"derivedFrom":makeQuery(id+"FM8r0xqs9yAwbjn_1.7.F5.opExtrude","CAP_EDGE",EDGE,{"disambiguationData":[OSD([sQuery(id+"F4.wireOp",EDGE,"E21")])],"isStart":true})});
            var Q55;
            Q55=makeQuery(id+"FM8r0xqs9yAwbjn_1.7.F5.boolean.opBoolean","COPY",EDGE,{"derivedFrom":makeQuery(id+"FM8r0xqs9yAwbjn_1.7.F5.opExtrude","CAP_EDGE",EDGE,{"disambiguationData":[OSD([sQuery(id+"F4.wireOp",EDGE,"E14")])],"isStart":true})});
            var Q56;
            Q56=makeQuery(id+"FM8r0xqs9yAwbjn_1.7.F5.boolean.opBoolean","COPY",EDGE,{"derivedFrom":makeQuery(id+"FM8r0xqs9yAwbjn_1.7.F5.opExtrude","SWEPT_EDGE",EDGE,{"disambiguationData":[OSD([sQuery(id+"F0.wireOp",EDGE,"E0"),sQuery(id+"F4.wireOp",EDGE,"E14"),sQuery(id+"F4.wireOp",EDGE,"E22.0")])]})});
            var Q57;
            Q57=makeQuery(id+"FM8r0xqs9yAwbjn_1.7.F5.boolean.opBoolean","COPY",EDGE,{"derivedFrom":makeQuery(id+"FM8r0xqs9yAwbjn_1.7.F5.opExtrude","SWEPT_EDGE",EDGE,{"disambiguationData":[OSD([sQuery(id+"F0.wireOp",EDGE,"E0"),sQuery(id+"F4.wireOp",EDGE,"E13"),sQuery(id+"F4.wireOp",EDGE,"E22.0")])]})});
            var Q58;
            Q58=makeQuery(id+"FM8r0xqs9yAwbjn_1.8.F5.boolean.opBoolean","COPY",EDGE,{"derivedFrom":makeQuery(id+"FM8r0xqs9yAwbjn_1.8.F5.opExtrude","CAP_EDGE",EDGE,{"disambiguationData":[OSD([sQuery(id+"F4.wireOp",EDGE,"E13")])],"isStart":true})});
            var Q59;
            Q59=makeQuery(id+"FM8r0xqs9yAwbjn_1.8.F5.boolean.opBoolean","COPY",EDGE,{"derivedFrom":makeQuery(id+"FM8r0xqs9yAwbjn_1.8.F5.opExtrude","CAP_EDGE",EDGE,{"disambiguationData":[OSD([sQuery(id+"F4.wireOp",EDGE,"E21")])],"isStart":true})});
            var Q60;
            Q60=makeQuery(id+"FM8r0xqs9yAwbjn_1.8.F5.boolean.opBoolean","COPY",EDGE,{"derivedFrom":makeQuery(id+"FM8r0xqs9yAwbjn_1.8.F5.opExtrude","CAP_EDGE",EDGE,{"disambiguationData":[OSD([sQuery(id+"F4.wireOp",EDGE,"E14")])],"isStart":true})});
            var Q61;
            Q61=makeQuery(id+"FM8r0xqs9yAwbjn_1.8.F5.boolean.opBoolean","COPY",EDGE,{"derivedFrom":makeQuery(id+"FM8r0xqs9yAwbjn_1.8.F5.opExtrude","SWEPT_EDGE",EDGE,{"disambiguationData":[OSD([sQuery(id+"F0.wireOp",EDGE,"E0"),sQuery(id+"F4.wireOp",EDGE,"E14"),sQuery(id+"F4.wireOp",EDGE,"E22.0")])]})});
            var Q62;
            Q62=makeQuery(id+"FM8r0xqs9yAwbjn_1.8.F5.boolean.opBoolean","COPY",EDGE,{"derivedFrom":makeQuery(id+"FM8r0xqs9yAwbjn_1.8.F5.opExtrude","SWEPT_EDGE",EDGE,{"disambiguationData":[OSD([sQuery(id+"F0.wireOp",EDGE,"E0"),sQuery(id+"F4.wireOp",EDGE,"E13"),sQuery(id+"F4.wireOp",EDGE,"E22.0")])]})});
            var Q63;
            {var subQ0=sQuery(id+"F0.wireOp",EDGE,"E0");var subQ3=sQuery(id+"F4.wireOp",EDGE,"E13");var subQ4=sQuery(id+"F4.wireOp",EDGE,"E14");var subQ5=makeQuery(id+"FM8r0xqs9yAwbjn_1.7.F5.opExtrude","SWEPT_FACE",FACE,{"disambiguationData":[OSD([subQ4])]});var subQ6=makeQuery(id+"F5.boolean.opBoolean","COPY",FACE,{"derivedFrom":makeQuery(id+"F5.opExtrude","SWEPT_FACE",FACE,{"disambiguationData":[OSD([subQ3])]})});Q63=makeQuery(id+"FM8r0xqs9yAwbjn_1.8.F5.boolean.opBoolean","SPLIT",EDGE,{"disambiguationData":[TD([makeQuery(id+"FM8r0xqs9yAwbjn_1.7.F5.boolean.opBoolean","COPY",FACE,{"derivedFrom":subQ5})])],"derivedFrom":makeQuery(id+"FM8r0xqs9yAwbjn_1.7.F5.boolean.opBoolean","SPLIT",EDGE,{"disambiguationData":[TD([subQ6])],"derivedFrom":makeQuery(id+"FM8r0xqs9yAwbjn_1.6.F5.boolean.opBoolean","SPLIT",EDGE,{"disambiguationData":[TD([subQ6])],"derivedFrom":makeQuery(id+"FM8r0xqs9yAwbjn_1.5.F5.boolean.opBoolean","SPLIT",EDGE,{"disambiguationData":[TD([subQ6])],"derivedFrom":makeQuery(id+"FM8r0xqs9yAwbjn_1.4.F5.boolean.opBoolean","SPLIT",EDGE,{"disambiguationData":[TD([subQ6])],"derivedFrom":makeQuery(id+"FM8r0xqs9yAwbjn_1.3.F5.boolean.opBoolean","SPLIT",EDGE,{"disambiguationData":[TD([subQ6])],"derivedFrom":makeQuery(id+"FM8r0xqs9yAwbjn_1.2.F5.boolean.opBoolean","SPLIT",EDGE,{"disambiguationData":[TD([subQ6])],"derivedFrom":makeQuery(id+"FM8r0xqs9yAwbjn_1.1.F5.boolean.opBoolean","SPLIT",EDGE,{"disambiguationData":[TD([subQ6])],"derivedFrom":makeQuery(id+"F1.opExtrude","CAP_EDGE",EDGE,{"disambiguationData":[OSD([subQ0])],"isStart":true})})})})})})})})});}
            var Q64;
            {var subQ0=sQuery(id+"F0.wireOp",EDGE,"E0");var subQ3=sQuery(id+"F4.wireOp",EDGE,"E14");var subQ4=makeQuery(id+"FM8r0xqs9yAwbjn_1.6.F5.opExtrude","SWEPT_FACE",FACE,{"disambiguationData":[OSD([subQ3])]});var subQ5=sQuery(id+"F4.wireOp",EDGE,"E13");var subQ6=makeQuery(id+"F5.boolean.opBoolean","COPY",FACE,{"derivedFrom":makeQuery(id+"F5.opExtrude","SWEPT_FACE",FACE,{"disambiguationData":[OSD([subQ5])]})});Q64=makeQuery(id+"FM8r0xqs9yAwbjn_1.7.F5.boolean.opBoolean","SPLIT",EDGE,{"disambiguationData":[TD([makeQuery(id+"FM8r0xqs9yAwbjn_1.6.F5.boolean.opBoolean","COPY",FACE,{"derivedFrom":subQ4})])],"derivedFrom":makeQuery(id+"FM8r0xqs9yAwbjn_1.6.F5.boolean.opBoolean","SPLIT",EDGE,{"disambiguationData":[TD([subQ6])],"derivedFrom":makeQuery(id+"FM8r0xqs9yAwbjn_1.5.F5.boolean.opBoolean","SPLIT",EDGE,{"disambiguationData":[TD([subQ6])],"derivedFrom":makeQuery(id+"FM8r0xqs9yAwbjn_1.4.F5.boolean.opBoolean","SPLIT",EDGE,{"disambiguationData":[TD([subQ6])],"derivedFrom":makeQuery(id+"FM8r0xqs9yAwbjn_1.3.F5.boolean.opBoolean","SPLIT",EDGE,{"disambiguationData":[TD([subQ6])],"derivedFrom":makeQuery(id+"FM8r0xqs9yAwbjn_1.2.F5.boolean.opBoolean","SPLIT",EDGE,{"disambiguationData":[TD([subQ6])],"derivedFrom":makeQuery(id+"FM8r0xqs9yAwbjn_1.1.F5.boolean.opBoolean","SPLIT",EDGE,{"disambiguationData":[TD([subQ6])],"derivedFrom":makeQuery(id+"F1.opExtrude","CAP_EDGE",EDGE,{"disambiguationData":[OSD([subQ0])],"isStart":true})})})})})})})});}
            var Q65;
            Q65=makeQuery(id+"FM8r0xqs9yAwbjn_1.9.F5.boolean.opBoolean","COPY",EDGE,{"derivedFrom":makeQuery(id+"FM8r0xqs9yAwbjn_1.9.F5.opExtrude","CAP_EDGE",EDGE,{"disambiguationData":[OSD([sQuery(id+"F4.wireOp",EDGE,"E21")])],"isStart":true})});
            var Q66;
            Q66=makeQuery(id+"FM8r0xqs9yAwbjn_1.9.F5.boolean.opBoolean","COPY",EDGE,{"derivedFrom":makeQuery(id+"FM8r0xqs9yAwbjn_1.9.F5.opExtrude","CAP_EDGE",EDGE,{"disambiguationData":[OSD([sQuery(id+"F4.wireOp",EDGE,"E13")])],"isStart":true})});
            var Q67;
            {var subQ0=sQuery(id+"F0.wireOp",EDGE,"E0");var subQ3=sQuery(id+"F4.wireOp",EDGE,"E13");var subQ4=sQuery(id+"F4.wireOp",EDGE,"E14");var subQ5=makeQuery(id+"FM8r0xqs9yAwbjn_1.8.F5.opExtrude","SWEPT_FACE",FACE,{"disambiguationData":[OSD([subQ4])]});var subQ6=makeQuery(id+"F5.boolean.opBoolean","COPY",FACE,{"derivedFrom":makeQuery(id+"F5.opExtrude","SWEPT_FACE",FACE,{"disambiguationData":[OSD([subQ3])]})});Q67=makeQuery(id+"FM8r0xqs9yAwbjn_1.9.F5.boolean.opBoolean","SPLIT",EDGE,{"disambiguationData":[TD([makeQuery(id+"FM8r0xqs9yAwbjn_1.8.F5.boolean.opBoolean","COPY",FACE,{"derivedFrom":subQ5})])],"derivedFrom":makeQuery(id+"FM8r0xqs9yAwbjn_1.8.F5.boolean.opBoolean","SPLIT",EDGE,{"disambiguationData":[TD([subQ6])],"derivedFrom":makeQuery(id+"FM8r0xqs9yAwbjn_1.7.F5.boolean.opBoolean","SPLIT",EDGE,{"disambiguationData":[TD([subQ6])],"derivedFrom":makeQuery(id+"FM8r0xqs9yAwbjn_1.6.F5.boolean.opBoolean","SPLIT",EDGE,{"disambiguationData":[TD([subQ6])],"derivedFrom":makeQuery(id+"FM8r0xqs9yAwbjn_1.5.F5.boolean.opBoolean","SPLIT",EDGE,{"disambiguationData":[TD([subQ6])],"derivedFrom":makeQuery(id+"FM8r0xqs9yAwbjn_1.4.F5.boolean.opBoolean","SPLIT",EDGE,{"disambiguationData":[TD([subQ6])],"derivedFrom":makeQuery(id+"FM8r0xqs9yAwbjn_1.3.F5.boolean.opBoolean","SPLIT",EDGE,{"disambiguationData":[TD([subQ6])],"derivedFrom":makeQuery(id+"FM8r0xqs9yAwbjn_1.2.F5.boolean.opBoolean","SPLIT",EDGE,{"disambiguationData":[TD([subQ6])],"derivedFrom":makeQuery(id+"FM8r0xqs9yAwbjn_1.1.F5.boolean.opBoolean","SPLIT",EDGE,{"disambiguationData":[TD([subQ6])],"derivedFrom":makeQuery(id+"F1.opExtrude","CAP_EDGE",EDGE,{"disambiguationData":[OSD([subQ0])],"isStart":true})})})})})})})})})});}
            var Q68;
            Q68=makeQuery(id+"FM8r0xqs9yAwbjn_1.9.F5.boolean.opBoolean","COPY",EDGE,{"derivedFrom":makeQuery(id+"FM8r0xqs9yAwbjn_1.9.F5.opExtrude","SWEPT_EDGE",EDGE,{"disambiguationData":[OSD([sQuery(id+"F0.wireOp",EDGE,"E0"),sQuery(id+"F4.wireOp",EDGE,"E13"),sQuery(id+"F4.wireOp",EDGE,"E22.0")])]})});
            var Q69;
            Q69=makeQuery(id+"FM8r0xqs9yAwbjn_1.9.F5.boolean.opBoolean","COPY",EDGE,{"derivedFrom":makeQuery(id+"FM8r0xqs9yAwbjn_1.9.F5.opExtrude","SWEPT_EDGE",EDGE,{"disambiguationData":[OSD([sQuery(id+"F0.wireOp",EDGE,"E0"),sQuery(id+"F4.wireOp",EDGE,"E14"),sQuery(id+"F4.wireOp",EDGE,"E22.0")])]})});
            var Q70;
            Q70=makeQuery(id+"FM8r0xqs9yAwbjn_1.9.F5.boolean.opBoolean","COPY",EDGE,{"derivedFrom":makeQuery(id+"FM8r0xqs9yAwbjn_1.9.F5.opExtrude","CAP_EDGE",EDGE,{"disambiguationData":[OSD([sQuery(id+"F4.wireOp",EDGE,"E14")])],"isStart":true})});
            var Q71;
            {var subQ0=sQuery(id+"F0.wireOp",EDGE,"E0");var subQ3=sQuery(id+"F4.wireOp",EDGE,"E14");var subQ4=makeQuery(id+"FM8r0xqs9yAwbjn_1.9.F5.opExtrude","SWEPT_FACE",FACE,{"disambiguationData":[OSD([subQ3])]});var subQ5=sQuery(id+"F4.wireOp",EDGE,"E13");var subQ6=makeQuery(id+"F5.boolean.opBoolean","COPY",FACE,{"derivedFrom":makeQuery(id+"F5.opExtrude","SWEPT_FACE",FACE,{"disambiguationData":[OSD([subQ5])]})});Q71=makeQuery(id+"FM8r0xqs9yAwbjn_1.10.F5.boolean.opBoolean","SPLIT",EDGE,{"disambiguationData":[TD([makeQuery(id+"FM8r0xqs9yAwbjn_1.9.F5.boolean.opBoolean","COPY",FACE,{"derivedFrom":subQ4})])],"derivedFrom":makeQuery(id+"FM8r0xqs9yAwbjn_1.9.F5.boolean.opBoolean","SPLIT",EDGE,{"disambiguationData":[TD([subQ6])],"derivedFrom":makeQuery(id+"FM8r0xqs9yAwbjn_1.8.F5.boolean.opBoolean","SPLIT",EDGE,{"disambiguationData":[TD([subQ6])],"derivedFrom":makeQuery(id+"FM8r0xqs9yAwbjn_1.7.F5.boolean.opBoolean","SPLIT",EDGE,{"disambiguationData":[TD([subQ6])],"derivedFrom":makeQuery(id+"FM8r0xqs9yAwbjn_1.6.F5.boolean.opBoolean","SPLIT",EDGE,{"disambiguationData":[TD([subQ6])],"derivedFrom":makeQuery(id+"FM8r0xqs9yAwbjn_1.5.F5.boolean.opBoolean","SPLIT",EDGE,{"disambiguationData":[TD([subQ6])],"derivedFrom":makeQuery(id+"FM8r0xqs9yAwbjn_1.4.F5.boolean.opBoolean","SPLIT",EDGE,{"disambiguationData":[TD([subQ6])],"derivedFrom":makeQuery(id+"FM8r0xqs9yAwbjn_1.3.F5.boolean.opBoolean","SPLIT",EDGE,{"disambiguationData":[TD([subQ6])],"derivedFrom":makeQuery(id+"FM8r0xqs9yAwbjn_1.2.F5.boolean.opBoolean","SPLIT",EDGE,{"disambiguationData":[TD([subQ6])],"derivedFrom":makeQuery(id+"FM8r0xqs9yAwbjn_1.1.F5.boolean.opBoolean","SPLIT",EDGE,{"disambiguationData":[TD([subQ6])],"derivedFrom":makeQuery(id+"F1.opExtrude","CAP_EDGE",EDGE,{"disambiguationData":[OSD([subQ0])],"isStart":true})})})})})})})})})})});}
            var Q72;
            Q72=makeQuery(id+"FM8r0xqs9yAwbjn_1.10.F5.boolean.opBoolean","COPY",EDGE,{"derivedFrom":makeQuery(id+"FM8r0xqs9yAwbjn_1.10.F5.opExtrude","CAP_EDGE",EDGE,{"disambiguationData":[OSD([sQuery(id+"F4.wireOp",EDGE,"E13")])],"isStart":true})});
            var Q73;
            Q73=makeQuery(id+"FM8r0xqs9yAwbjn_1.10.F5.boolean.opBoolean","COPY",EDGE,{"derivedFrom":makeQuery(id+"FM8r0xqs9yAwbjn_1.10.F5.opExtrude","CAP_EDGE",EDGE,{"disambiguationData":[OSD([sQuery(id+"F4.wireOp",EDGE,"E21")])],"isStart":true})});
            var Q74;
            Q74=makeQuery(id+"FM8r0xqs9yAwbjn_1.10.F5.boolean.opBoolean","COPY",EDGE,{"derivedFrom":makeQuery(id+"FM8r0xqs9yAwbjn_1.10.F5.opExtrude","CAP_EDGE",EDGE,{"disambiguationData":[OSD([sQuery(id+"F4.wireOp",EDGE,"E14")])],"isStart":true})});
            var Q75;
            Q75=makeQuery(id+"FM8r0xqs9yAwbjn_1.10.F5.boolean.opBoolean","COPY",EDGE,{"derivedFrom":makeQuery(id+"FM8r0xqs9yAwbjn_1.10.F5.opExtrude","SWEPT_EDGE",EDGE,{"disambiguationData":[OSD([sQuery(id+"F0.wireOp",EDGE,"E0"),sQuery(id+"F4.wireOp",EDGE,"E14"),sQuery(id+"F4.wireOp",EDGE,"E22.0")])]})});
            var Q76;
            Q76=makeQuery(id+"FM8r0xqs9yAwbjn_1.10.F5.boolean.opBoolean","COPY",EDGE,{"derivedFrom":makeQuery(id+"FM8r0xqs9yAwbjn_1.10.F5.opExtrude","SWEPT_EDGE",EDGE,{"disambiguationData":[OSD([sQuery(id+"F0.wireOp",EDGE,"E0"),sQuery(id+"F4.wireOp",EDGE,"E13"),sQuery(id+"F4.wireOp",EDGE,"E22.0")])]})});
            var Q77;
            {var subQ0=sQuery(id+"F0.wireOp",EDGE,"E0");var subQ3=sQuery(id+"F4.wireOp",EDGE,"E14");var subQ4=makeQuery(id+"FM8r0xqs9yAwbjn_1.10.F5.opExtrude","SWEPT_FACE",FACE,{"disambiguationData":[OSD([subQ3])]});var subQ5=sQuery(id+"F4.wireOp",EDGE,"E13");var subQ6=makeQuery(id+"F5.boolean.opBoolean","COPY",FACE,{"derivedFrom":makeQuery(id+"F5.opExtrude","SWEPT_FACE",FACE,{"disambiguationData":[OSD([subQ5])]})});Q77=makeQuery(id+"FM8r0xqs9yAwbjn_1.11.F5.boolean.opBoolean","SPLIT",EDGE,{"disambiguationData":[TD([makeQuery(id+"FM8r0xqs9yAwbjn_1.10.F5.boolean.opBoolean","COPY",FACE,{"derivedFrom":subQ4})])],"derivedFrom":makeQuery(id+"FM8r0xqs9yAwbjn_1.10.F5.boolean.opBoolean","SPLIT",EDGE,{"disambiguationData":[TD([subQ6])],"derivedFrom":makeQuery(id+"FM8r0xqs9yAwbjn_1.9.F5.boolean.opBoolean","SPLIT",EDGE,{"disambiguationData":[TD([subQ6])],"derivedFrom":makeQuery(id+"FM8r0xqs9yAwbjn_1.8.F5.boolean.opBoolean","SPLIT",EDGE,{"disambiguationData":[TD([subQ6])],"derivedFrom":makeQuery(id+"FM8r0xqs9yAwbjn_1.7.F5.boolean.opBoolean","SPLIT",EDGE,{"disambiguationData":[TD([subQ6])],"derivedFrom":makeQuery(id+"FM8r0xqs9yAwbjn_1.6.F5.boolean.opBoolean","SPLIT",EDGE,{"disambiguationData":[TD([subQ6])],"derivedFrom":makeQuery(id+"FM8r0xqs9yAwbjn_1.5.F5.boolean.opBoolean","SPLIT",EDGE,{"disambiguationData":[TD([subQ6])],"derivedFrom":makeQuery(id+"FM8r0xqs9yAwbjn_1.4.F5.boolean.opBoolean","SPLIT",EDGE,{"disambiguationData":[TD([subQ6])],"derivedFrom":makeQuery(id+"FM8r0xqs9yAwbjn_1.3.F5.boolean.opBoolean","SPLIT",EDGE,{"disambiguationData":[TD([subQ6])],"derivedFrom":makeQuery(id+"FM8r0xqs9yAwbjn_1.2.F5.boolean.opBoolean","SPLIT",EDGE,{"disambiguationData":[TD([subQ6])],"derivedFrom":makeQuery(id+"FM8r0xqs9yAwbjn_1.1.F5.boolean.opBoolean","SPLIT",EDGE,{"disambiguationData":[TD([subQ6])],"derivedFrom":makeQuery(id+"F1.opExtrude","CAP_EDGE",EDGE,{"disambiguationData":[OSD([subQ0])],"isStart":true})})})})})})})})})})})});}
            var Q78;
            Q78=makeQuery(id+"FM8r0xqs9yAwbjn_1.11.F5.boolean.opBoolean","COPY",EDGE,{"derivedFrom":makeQuery(id+"FM8r0xqs9yAwbjn_1.11.F5.opExtrude","CAP_EDGE",EDGE,{"disambiguationData":[OSD([sQuery(id+"F4.wireOp",EDGE,"E13")])],"isStart":true})});
            var Q79;
            Q79=makeQuery(id+"FM8r0xqs9yAwbjn_1.11.F5.boolean.opBoolean","COPY",EDGE,{"derivedFrom":makeQuery(id+"FM8r0xqs9yAwbjn_1.11.F5.opExtrude","CAP_EDGE",EDGE,{"disambiguationData":[OSD([sQuery(id+"F4.wireOp",EDGE,"E21")])],"isStart":true})});
            var Q80;
            Q80=makeQuery(id+"FM8r0xqs9yAwbjn_1.11.F5.boolean.opBoolean","COPY",EDGE,{"derivedFrom":makeQuery(id+"FM8r0xqs9yAwbjn_1.11.F5.opExtrude","CAP_EDGE",EDGE,{"disambiguationData":[OSD([sQuery(id+"F4.wireOp",EDGE,"E14")])],"isStart":true})});
            var Q81;
            Q81=makeQuery(id+"FM8r0xqs9yAwbjn_1.11.F5.boolean.opBoolean","COPY",EDGE,{"derivedFrom":makeQuery(id+"FM8r0xqs9yAwbjn_1.11.F5.opExtrude","SWEPT_EDGE",EDGE,{"disambiguationData":[OSD([sQuery(id+"F0.wireOp",EDGE,"E0"),sQuery(id+"F4.wireOp",EDGE,"E14"),sQuery(id+"F4.wireOp",EDGE,"E22.0")])]})});
            var Q82;
            Q82=makeQuery(id+"FM8r0xqs9yAwbjn_1.11.F5.boolean.opBoolean","COPY",EDGE,{"derivedFrom":makeQuery(id+"FM8r0xqs9yAwbjn_1.11.F5.opExtrude","SWEPT_EDGE",EDGE,{"disambiguationData":[OSD([sQuery(id+"F0.wireOp",EDGE,"E0"),sQuery(id+"F4.wireOp",EDGE,"E13"),sQuery(id+"F4.wireOp",EDGE,"E22.0")])]})});
            var Q83;
            Q83=makeQuery(id+"FM8r0xqs9yAwbjn_1.12.F5.boolean.opBoolean","COPY",EDGE,{"derivedFrom":makeQuery(id+"FM8r0xqs9yAwbjn_1.12.F5.opExtrude","SWEPT_EDGE",EDGE,{"disambiguationData":[OSD([sQuery(id+"F0.wireOp",EDGE,"E0"),sQuery(id+"F4.wireOp",EDGE,"E13"),sQuery(id+"F4.wireOp",EDGE,"E22.0")])]})});
            var Q84;
            Q84=makeQuery(id+"FM8r0xqs9yAwbjn_1.12.F5.boolean.opBoolean","COPY",EDGE,{"derivedFrom":makeQuery(id+"FM8r0xqs9yAwbjn_1.12.F5.opExtrude","CAP_EDGE",EDGE,{"disambiguationData":[OSD([sQuery(id+"F4.wireOp",EDGE,"E13")])],"isStart":true})});
            var Q85;
            Q85=makeQuery(id+"FM8r0xqs9yAwbjn_1.12.F5.boolean.opBoolean","COPY",EDGE,{"derivedFrom":makeQuery(id+"FM8r0xqs9yAwbjn_1.12.F5.opExtrude","CAP_EDGE",EDGE,{"disambiguationData":[OSD([sQuery(id+"F4.wireOp",EDGE,"E21")])],"isStart":true})});
            var Q86;
            Q86=makeQuery(id+"FM8r0xqs9yAwbjn_1.12.F5.boolean.opBoolean","COPY",EDGE,{"derivedFrom":makeQuery(id+"FM8r0xqs9yAwbjn_1.12.F5.opExtrude","CAP_EDGE",EDGE,{"disambiguationData":[OSD([sQuery(id+"F4.wireOp",EDGE,"E14")])],"isStart":true})});
            var Q87;
            Q87=makeQuery(id+"FM8r0xqs9yAwbjn_1.12.F5.boolean.opBoolean","COPY",EDGE,{"derivedFrom":makeQuery(id+"FM8r0xqs9yAwbjn_1.12.F5.opExtrude","SWEPT_EDGE",EDGE,{"disambiguationData":[OSD([sQuery(id+"F0.wireOp",EDGE,"E0"),sQuery(id+"F4.wireOp",EDGE,"E14"),sQuery(id+"F4.wireOp",EDGE,"E22.0")])]})});
            var Q88;
            Q88=makeQuery(id+"FM8r0xqs9yAwbjn_1.13.F5.boolean.opBoolean","COPY",EDGE,{"derivedFrom":makeQuery(id+"FM8r0xqs9yAwbjn_1.13.F5.opExtrude","CAP_EDGE",EDGE,{"disambiguationData":[OSD([sQuery(id+"F4.wireOp",EDGE,"E21")])],"isStart":true})});
            var Q89;
            Q89=makeQuery(id+"FM8r0xqs9yAwbjn_1.13.F5.boolean.opBoolean","COPY",EDGE,{"derivedFrom":makeQuery(id+"FM8r0xqs9yAwbjn_1.13.F5.opExtrude","CAP_EDGE",EDGE,{"disambiguationData":[OSD([sQuery(id+"F4.wireOp",EDGE,"E14")])],"isStart":true})});
            var Q90;
            Q90=makeQuery(id+"FM8r0xqs9yAwbjn_1.13.F5.boolean.opBoolean","COPY",EDGE,{"derivedFrom":makeQuery(id+"FM8r0xqs9yAwbjn_1.13.F5.opExtrude","SWEPT_EDGE",EDGE,{"disambiguationData":[OSD([sQuery(id+"F0.wireOp",EDGE,"E0"),sQuery(id+"F4.wireOp",EDGE,"E14"),sQuery(id+"F4.wireOp",EDGE,"E22.0")])]})});
            var Q91;
            Q91=makeQuery(id+"FM8r0xqs9yAwbjn_1.13.F5.boolean.opBoolean","COPY",EDGE,{"derivedFrom":makeQuery(id+"FM8r0xqs9yAwbjn_1.13.F5.opExtrude","SWEPT_EDGE",EDGE,{"disambiguationData":[OSD([sQuery(id+"F0.wireOp",EDGE,"E0"),sQuery(id+"F4.wireOp",EDGE,"E13"),sQuery(id+"F4.wireOp",EDGE,"E22.0")])]})});
            var Q92;
            {var subQ0=sQuery(id+"F0.wireOp",EDGE,"E0");var subQ3=sQuery(id+"F4.wireOp",EDGE,"E14");var subQ4=makeQuery(id+"FM8r0xqs9yAwbjn_1.12.F5.opExtrude","SWEPT_FACE",FACE,{"disambiguationData":[OSD([subQ3])]});var subQ5=sQuery(id+"F4.wireOp",EDGE,"E13");var subQ6=makeQuery(id+"F5.boolean.opBoolean","COPY",FACE,{"derivedFrom":makeQuery(id+"F5.opExtrude","SWEPT_FACE",FACE,{"disambiguationData":[OSD([subQ5])]})});Q92=makeQuery(id+"FM8r0xqs9yAwbjn_1.13.F5.boolean.opBoolean","SPLIT",EDGE,{"disambiguationData":[TD([makeQuery(id+"FM8r0xqs9yAwbjn_1.12.F5.boolean.opBoolean","COPY",FACE,{"derivedFrom":subQ4})])],"derivedFrom":makeQuery(id+"FM8r0xqs9yAwbjn_1.12.F5.boolean.opBoolean","SPLIT",EDGE,{"disambiguationData":[TD([subQ6])],"derivedFrom":makeQuery(id+"FM8r0xqs9yAwbjn_1.11.F5.boolean.opBoolean","SPLIT",EDGE,{"disambiguationData":[TD([subQ6])],"derivedFrom":makeQuery(id+"FM8r0xqs9yAwbjn_1.10.F5.boolean.opBoolean","SPLIT",EDGE,{"disambiguationData":[TD([subQ6])],"derivedFrom":makeQuery(id+"FM8r0xqs9yAwbjn_1.9.F5.boolean.opBoolean","SPLIT",EDGE,{"disambiguationData":[TD([subQ6])],"derivedFrom":makeQuery(id+"FM8r0xqs9yAwbjn_1.8.F5.boolean.opBoolean","SPLIT",EDGE,{"disambiguationData":[TD([subQ6])],"derivedFrom":makeQuery(id+"FM8r0xqs9yAwbjn_1.7.F5.boolean.opBoolean","SPLIT",EDGE,{"disambiguationData":[TD([subQ6])],"derivedFrom":makeQuery(id+"FM8r0xqs9yAwbjn_1.6.F5.boolean.opBoolean","SPLIT",EDGE,{"disambiguationData":[TD([subQ6])],"derivedFrom":makeQuery(id+"FM8r0xqs9yAwbjn_1.5.F5.boolean.opBoolean","SPLIT",EDGE,{"disambiguationData":[TD([subQ6])],"derivedFrom":makeQuery(id+"FM8r0xqs9yAwbjn_1.4.F5.boolean.opBoolean","SPLIT",EDGE,{"disambiguationData":[TD([subQ6])],"derivedFrom":makeQuery(id+"FM8r0xqs9yAwbjn_1.3.F5.boolean.opBoolean","SPLIT",EDGE,{"disambiguationData":[TD([subQ6])],"derivedFrom":makeQuery(id+"FM8r0xqs9yAwbjn_1.2.F5.boolean.opBoolean","SPLIT",EDGE,{"disambiguationData":[TD([subQ6])],"derivedFrom":makeQuery(id+"FM8r0xqs9yAwbjn_1.1.F5.boolean.opBoolean","SPLIT",EDGE,{"disambiguationData":[TD([subQ6])],"derivedFrom":makeQuery(id+"F1.opExtrude","CAP_EDGE",EDGE,{"disambiguationData":[OSD([subQ0])],"isStart":true})})})})})})})})})})})})})});}
            var Q93;
            {var subQ0=sQuery(id+"F0.wireOp",EDGE,"E0");var subQ3=sQuery(id+"F4.wireOp",EDGE,"E14");var subQ4=makeQuery(id+"FM8r0xqs9yAwbjn_1.11.F5.opExtrude","SWEPT_FACE",FACE,{"disambiguationData":[OSD([subQ3])]});var subQ5=sQuery(id+"F4.wireOp",EDGE,"E13");var subQ6=makeQuery(id+"F5.boolean.opBoolean","COPY",FACE,{"derivedFrom":makeQuery(id+"F5.opExtrude","SWEPT_FACE",FACE,{"disambiguationData":[OSD([subQ5])]})});Q93=makeQuery(id+"FM8r0xqs9yAwbjn_1.12.F5.boolean.opBoolean","SPLIT",EDGE,{"disambiguationData":[TD([makeQuery(id+"FM8r0xqs9yAwbjn_1.11.F5.boolean.opBoolean","COPY",FACE,{"derivedFrom":subQ4})])],"derivedFrom":makeQuery(id+"FM8r0xqs9yAwbjn_1.11.F5.boolean.opBoolean","SPLIT",EDGE,{"disambiguationData":[TD([subQ6])],"derivedFrom":makeQuery(id+"FM8r0xqs9yAwbjn_1.10.F5.boolean.opBoolean","SPLIT",EDGE,{"disambiguationData":[TD([subQ6])],"derivedFrom":makeQuery(id+"FM8r0xqs9yAwbjn_1.9.F5.boolean.opBoolean","SPLIT",EDGE,{"disambiguationData":[TD([subQ6])],"derivedFrom":makeQuery(id+"FM8r0xqs9yAwbjn_1.8.F5.boolean.opBoolean","SPLIT",EDGE,{"disambiguationData":[TD([subQ6])],"derivedFrom":makeQuery(id+"FM8r0xqs9yAwbjn_1.7.F5.boolean.opBoolean","SPLIT",EDGE,{"disambiguationData":[TD([subQ6])],"derivedFrom":makeQuery(id+"FM8r0xqs9yAwbjn_1.6.F5.boolean.opBoolean","SPLIT",EDGE,{"disambiguationData":[TD([subQ6])],"derivedFrom":makeQuery(id+"FM8r0xqs9yAwbjn_1.5.F5.boolean.opBoolean","SPLIT",EDGE,{"disambiguationData":[TD([subQ6])],"derivedFrom":makeQuery(id+"FM8r0xqs9yAwbjn_1.4.F5.boolean.opBoolean","SPLIT",EDGE,{"disambiguationData":[TD([subQ6])],"derivedFrom":makeQuery(id+"FM8r0xqs9yAwbjn_1.3.F5.boolean.opBoolean","SPLIT",EDGE,{"disambiguationData":[TD([subQ6])],"derivedFrom":makeQuery(id+"FM8r0xqs9yAwbjn_1.2.F5.boolean.opBoolean","SPLIT",EDGE,{"disambiguationData":[TD([subQ6])],"derivedFrom":makeQuery(id+"FM8r0xqs9yAwbjn_1.1.F5.boolean.opBoolean","SPLIT",EDGE,{"disambiguationData":[TD([subQ6])],"derivedFrom":makeQuery(id+"F1.opExtrude","CAP_EDGE",EDGE,{"disambiguationData":[OSD([subQ0])],"isStart":true})})})})})})})})})})})})});}
            var Q94;
            {var subQ0=sQuery(id+"F0.wireOp",EDGE,"E0");var subQ3=sQuery(id+"F4.wireOp",EDGE,"E14");var subQ4=makeQuery(id+"FM8r0xqs9yAwbjn_1.13.F5.opExtrude","SWEPT_FACE",FACE,{"disambiguationData":[OSD([subQ3])]});var subQ5=sQuery(id+"F4.wireOp",EDGE,"E13");var subQ6=makeQuery(id+"F5.boolean.opBoolean","COPY",FACE,{"derivedFrom":makeQuery(id+"F5.opExtrude","SWEPT_FACE",FACE,{"disambiguationData":[OSD([subQ5])]})});Q94=makeQuery(id+"FM8r0xqs9yAwbjn_1.14.F5.boolean.opBoolean","SPLIT",EDGE,{"disambiguationData":[TD([makeQuery(id+"FM8r0xqs9yAwbjn_1.13.F5.boolean.opBoolean","COPY",FACE,{"derivedFrom":subQ4})])],"derivedFrom":makeQuery(id+"FM8r0xqs9yAwbjn_1.13.F5.boolean.opBoolean","SPLIT",EDGE,{"disambiguationData":[TD([subQ6])],"derivedFrom":makeQuery(id+"FM8r0xqs9yAwbjn_1.12.F5.boolean.opBoolean","SPLIT",EDGE,{"disambiguationData":[TD([subQ6])],"derivedFrom":makeQuery(id+"FM8r0xqs9yAwbjn_1.11.F5.boolean.opBoolean","SPLIT",EDGE,{"disambiguationData":[TD([subQ6])],"derivedFrom":makeQuery(id+"FM8r0xqs9yAwbjn_1.10.F5.boolean.opBoolean","SPLIT",EDGE,{"disambiguationData":[TD([subQ6])],"derivedFrom":makeQuery(id+"FM8r0xqs9yAwbjn_1.9.F5.boolean.opBoolean","SPLIT",EDGE,{"disambiguationData":[TD([subQ6])],"derivedFrom":makeQuery(id+"FM8r0xqs9yAwbjn_1.8.F5.boolean.opBoolean","SPLIT",EDGE,{"disambiguationData":[TD([subQ6])],"derivedFrom":makeQuery(id+"FM8r0xqs9yAwbjn_1.7.F5.boolean.opBoolean","SPLIT",EDGE,{"disambiguationData":[TD([subQ6])],"derivedFrom":makeQuery(id+"FM8r0xqs9yAwbjn_1.6.F5.boolean.opBoolean","SPLIT",EDGE,{"disambiguationData":[TD([subQ6])],"derivedFrom":makeQuery(id+"FM8r0xqs9yAwbjn_1.5.F5.boolean.opBoolean","SPLIT",EDGE,{"disambiguationData":[TD([subQ6])],"derivedFrom":makeQuery(id+"FM8r0xqs9yAwbjn_1.4.F5.boolean.opBoolean","SPLIT",EDGE,{"disambiguationData":[TD([subQ6])],"derivedFrom":makeQuery(id+"FM8r0xqs9yAwbjn_1.3.F5.boolean.opBoolean","SPLIT",EDGE,{"disambiguationData":[TD([subQ6])],"derivedFrom":makeQuery(id+"FM8r0xqs9yAwbjn_1.2.F5.boolean.opBoolean","SPLIT",EDGE,{"disambiguationData":[TD([subQ6])],"derivedFrom":makeQuery(id+"FM8r0xqs9yAwbjn_1.1.F5.boolean.opBoolean","SPLIT",EDGE,{"disambiguationData":[TD([subQ6])],"derivedFrom":makeQuery(id+"F1.opExtrude","CAP_EDGE",EDGE,{"disambiguationData":[OSD([subQ0])],"isStart":true})})})})})})})})})})})})})})});}
            var Q95;
            {var subQ0=sQuery(id+"F0.wireOp",EDGE,"E0");var subQ3=sQuery(id+"F4.wireOp",EDGE,"E14");var subQ4=makeQuery(id+"FM8r0xqs9yAwbjn_1.14.F5.opExtrude","SWEPT_FACE",FACE,{"disambiguationData":[OSD([subQ3])]});var subQ5=sQuery(id+"F4.wireOp",EDGE,"E13");var subQ6=makeQuery(id+"F5.boolean.opBoolean","COPY",FACE,{"derivedFrom":makeQuery(id+"F5.opExtrude","SWEPT_FACE",FACE,{"disambiguationData":[OSD([subQ5])]})});Q95=makeQuery(id+"FM8r0xqs9yAwbjn_1.15.F5.boolean.opBoolean","SPLIT",EDGE,{"disambiguationData":[TD([makeQuery(id+"FM8r0xqs9yAwbjn_1.14.F5.boolean.opBoolean","COPY",FACE,{"derivedFrom":subQ4})])],"derivedFrom":makeQuery(id+"FM8r0xqs9yAwbjn_1.14.F5.boolean.opBoolean","SPLIT",EDGE,{"disambiguationData":[TD([subQ6])],"derivedFrom":makeQuery(id+"FM8r0xqs9yAwbjn_1.13.F5.boolean.opBoolean","SPLIT",EDGE,{"disambiguationData":[TD([subQ6])],"derivedFrom":makeQuery(id+"FM8r0xqs9yAwbjn_1.12.F5.boolean.opBoolean","SPLIT",EDGE,{"disambiguationData":[TD([subQ6])],"derivedFrom":makeQuery(id+"FM8r0xqs9yAwbjn_1.11.F5.boolean.opBoolean","SPLIT",EDGE,{"disambiguationData":[TD([subQ6])],"derivedFrom":makeQuery(id+"FM8r0xqs9yAwbjn_1.10.F5.boolean.opBoolean","SPLIT",EDGE,{"disambiguationData":[TD([subQ6])],"derivedFrom":makeQuery(id+"FM8r0xqs9yAwbjn_1.9.F5.boolean.opBoolean","SPLIT",EDGE,{"disambiguationData":[TD([subQ6])],"derivedFrom":makeQuery(id+"FM8r0xqs9yAwbjn_1.8.F5.boolean.opBoolean","SPLIT",EDGE,{"disambiguationData":[TD([subQ6])],"derivedFrom":makeQuery(id+"FM8r0xqs9yAwbjn_1.7.F5.boolean.opBoolean","SPLIT",EDGE,{"disambiguationData":[TD([subQ6])],"derivedFrom":makeQuery(id+"FM8r0xqs9yAwbjn_1.6.F5.boolean.opBoolean","SPLIT",EDGE,{"disambiguationData":[TD([subQ6])],"derivedFrom":makeQuery(id+"FM8r0xqs9yAwbjn_1.5.F5.boolean.opBoolean","SPLIT",EDGE,{"disambiguationData":[TD([subQ6])],"derivedFrom":makeQuery(id+"FM8r0xqs9yAwbjn_1.4.F5.boolean.opBoolean","SPLIT",EDGE,{"disambiguationData":[TD([subQ6])],"derivedFrom":makeQuery(id+"FM8r0xqs9yAwbjn_1.3.F5.boolean.opBoolean","SPLIT",EDGE,{"disambiguationData":[TD([subQ6])],"derivedFrom":makeQuery(id+"FM8r0xqs9yAwbjn_1.2.F5.boolean.opBoolean","SPLIT",EDGE,{"disambiguationData":[TD([subQ6])],"derivedFrom":makeQuery(id+"FM8r0xqs9yAwbjn_1.1.F5.boolean.opBoolean","SPLIT",EDGE,{"disambiguationData":[TD([subQ6])],"derivedFrom":makeQuery(id+"F1.opExtrude","CAP_EDGE",EDGE,{"disambiguationData":[OSD([subQ0])],"isStart":true})})})})})})})})})})})})})})})});}
            var Q96;
            Q96=makeQuery(id+"FM8r0xqs9yAwbjn_1.15.F5.boolean.opBoolean","COPY",EDGE,{"derivedFrom":makeQuery(id+"FM8r0xqs9yAwbjn_1.15.F5.opExtrude","CAP_EDGE",EDGE,{"disambiguationData":[OSD([sQuery(id+"F4.wireOp",EDGE,"E21")])],"isStart":true})});
            var Q97;
            Q97=makeQuery(id+"FM8r0xqs9yAwbjn_1.15.F5.boolean.opBoolean","COPY",EDGE,{"derivedFrom":makeQuery(id+"FM8r0xqs9yAwbjn_1.15.F5.opExtrude","CAP_EDGE",EDGE,{"disambiguationData":[OSD([sQuery(id+"F4.wireOp",EDGE,"E14")])],"isStart":true})});
            var Q98;
            Q98=makeQuery(id+"FM8r0xqs9yAwbjn_1.15.F5.boolean.opBoolean","COPY",EDGE,{"derivedFrom":makeQuery(id+"FM8r0xqs9yAwbjn_1.15.F5.opExtrude","CAP_EDGE",EDGE,{"disambiguationData":[OSD([sQuery(id+"F4.wireOp",EDGE,"E13")])],"isStart":true})});
            var Q99;
            Q99=makeQuery(id+"FM8r0xqs9yAwbjn_1.15.F5.boolean.opBoolean","COPY",EDGE,{"derivedFrom":makeQuery(id+"FM8r0xqs9yAwbjn_1.15.F5.opExtrude","SWEPT_EDGE",EDGE,{"disambiguationData":[OSD([sQuery(id+"F0.wireOp",EDGE,"E0"),sQuery(id+"F4.wireOp",EDGE,"E14"),sQuery(id+"F4.wireOp",EDGE,"E22.0")])]})});
            var Q100;
            Q100=makeQuery(id+"FM8r0xqs9yAwbjn_1.15.F5.boolean.opBoolean","COPY",EDGE,{"derivedFrom":makeQuery(id+"FM8r0xqs9yAwbjn_1.15.F5.opExtrude","SWEPT_EDGE",EDGE,{"disambiguationData":[OSD([sQuery(id+"F0.wireOp",EDGE,"E0"),sQuery(id+"F4.wireOp",EDGE,"E13"),sQuery(id+"F4.wireOp",EDGE,"E22.0")])]})});
            var Q101;
            Q101=makeQuery(id+"FM8r0xqs9yAwbjn_1.14.F5.boolean.opBoolean","COPY",EDGE,{"derivedFrom":makeQuery(id+"FM8r0xqs9yAwbjn_1.14.F5.opExtrude","SWEPT_EDGE",EDGE,{"disambiguationData":[OSD([sQuery(id+"F0.wireOp",EDGE,"E0"),sQuery(id+"F4.wireOp",EDGE,"E14"),sQuery(id+"F4.wireOp",EDGE,"E22.0")])]})});
            var Q102;
            Q102=makeQuery(id+"FM8r0xqs9yAwbjn_1.14.F5.boolean.opBoolean","COPY",EDGE,{"derivedFrom":makeQuery(id+"FM8r0xqs9yAwbjn_1.14.F5.opExtrude","CAP_EDGE",EDGE,{"disambiguationData":[OSD([sQuery(id+"F4.wireOp",EDGE,"E14")])],"isStart":true})});
            var Q103;
            Q103=makeQuery(id+"FM8r0xqs9yAwbjn_1.14.F5.boolean.opBoolean","COPY",EDGE,{"derivedFrom":makeQuery(id+"FM8r0xqs9yAwbjn_1.14.F5.opExtrude","CAP_EDGE",EDGE,{"disambiguationData":[OSD([sQuery(id+"F4.wireOp",EDGE,"E21")])],"isStart":true})});
            var Q104;
            Q104=makeQuery(id+"FM8r0xqs9yAwbjn_1.14.F5.boolean.opBoolean","COPY",EDGE,{"derivedFrom":makeQuery(id+"FM8r0xqs9yAwbjn_1.14.F5.opExtrude","CAP_EDGE",EDGE,{"disambiguationData":[OSD([sQuery(id+"F4.wireOp",EDGE,"E13")])],"isStart":true})});
            var Q105;
            Q105=makeQuery(id+"FM8r0xqs9yAwbjn_1.14.F5.boolean.opBoolean","COPY",EDGE,{"derivedFrom":makeQuery(id+"FM8r0xqs9yAwbjn_1.14.F5.opExtrude","SWEPT_EDGE",EDGE,{"disambiguationData":[OSD([sQuery(id+"F0.wireOp",EDGE,"E0"),sQuery(id+"F4.wireOp",EDGE,"E13"),sQuery(id+"F4.wireOp",EDGE,"E22.0")])]})});
            var Q106;
            Q106=makeQuery(id+"FM8r0xqs9yAwbjn_1.13.F5.boolean.opBoolean","COPY",EDGE,{"derivedFrom":makeQuery(id+"FM8r0xqs9yAwbjn_1.13.F5.opExtrude","CAP_EDGE",EDGE,{"disambiguationData":[OSD([sQuery(id+"F4.wireOp",EDGE,"E13")])],"isStart":true})});
            var Q107;
            Q107=makeQuery(id+"FM8r0xqs9yAwbjn_1.3.F5.boolean.opBoolean","COPY",EDGE,{"derivedFrom":makeQuery(id+"FM8r0xqs9yAwbjn_1.3.F5.opExtrude","CAP_EDGE",EDGE,{"disambiguationData":[OSD([sQuery(id+"F4.wireOp",EDGE,"E14")])],"isStart":true})});
            fillet(context, id + "F6", {"entities" : qUnion([Q0, Q1, Q2, Q3, Q4, Q5, Q6, Q7, Q8, Q9, Q10, Q11, Q12, Q13, Q14, Q15, Q16, Q17, Q18, Q19, Q20, Q21, Q22, Q23, Q24, Q25, Q26, Q27, Q28, Q29, Q30, Q31, Q32, Q33, Q34, Q35, Q36, Q37, Q38, Q39, Q40, Q41, Q42, Q43, Q44, Q45, Q46, Q47, Q48, Q49, Q50, Q51, Q52, Q53, Q54, Q55, Q56, Q57, Q58, Q59, Q60, Q61, Q62, Q63, Q64, Q65, Q66, Q67, Q68, Q69, Q70, Q71, Q72, Q73, Q74, Q75, Q76, Q77, Q78, Q79, Q80, Q81, Q82, Q83, Q84, Q85, Q86, Q87, Q88, Q89, Q90, Q91, Q92, Q93, Q94, Q95, Q96, Q97, Q98, Q99, Q100, Q101, Q102, Q103, Q104, Q105, Q106, Q107]), "radius" : .2 * mm, "tangentPropagation" : true, "allowEdgeOverflow" : false});
        }
        {
            var Q0;
            {var subQ0=sQuery(id+"F0.wireOp",EDGE,"E0");var subQ4=makeQuery(id+"F3.boolean.opBoolean","COPY",FACE,{"derivedFrom":makeQuery(id+"F3.opExtrude","SWEPT_FACE",FACE,{"disambiguationData":[OSD([sQuery(id+"F2.wireOp",EDGE,"E3")])]})});Q0=makeQuery(id+"FMRX2liYoJm4zaX_1.17.F3.boolean.opBoolean","SPLIT",EDGE,{"disambiguationData":[TD([subQ4])],"derivedFrom":makeQuery(id+"FMRX2liYoJm4zaX_1.16.F3.boolean.opBoolean","SPLIT",EDGE,{"disambiguationData":[TD([subQ4])],"derivedFrom":makeQuery(id+"FMRX2liYoJm4zaX_1.15.F3.boolean.opBoolean","SPLIT",EDGE,{"disambiguationData":[TD([subQ4])],"derivedFrom":makeQuery(id+"FMRX2liYoJm4zaX_1.14.F3.boolean.opBoolean","SPLIT",EDGE,{"disambiguationData":[TD([subQ4])],"derivedFrom":makeQuery(id+"FMRX2liYoJm4zaX_1.13.F3.boolean.opBoolean","SPLIT",EDGE,{"disambiguationData":[TD([subQ4])],"derivedFrom":makeQuery(id+"FMRX2liYoJm4zaX_1.12.F3.boolean.opBoolean","SPLIT",EDGE,{"disambiguationData":[TD([subQ4])],"derivedFrom":makeQuery(id+"FMRX2liYoJm4zaX_1.11.F3.boolean.opBoolean","SPLIT",EDGE,{"disambiguationData":[TD([subQ4])],"derivedFrom":makeQuery(id+"FMRX2liYoJm4zaX_1.10.F3.boolean.opBoolean","SPLIT",EDGE,{"disambiguationData":[TD([subQ4])],"derivedFrom":makeQuery(id+"FMRX2liYoJm4zaX_1.9.F3.boolean.opBoolean","SPLIT",EDGE,{"disambiguationData":[TD([subQ4])],"derivedFrom":makeQuery(id+"FMRX2liYoJm4zaX_1.8.F3.boolean.opBoolean","SPLIT",EDGE,{"disambiguationData":[TD([subQ4])],"derivedFrom":makeQuery(id+"FMRX2liYoJm4zaX_1.7.F3.boolean.opBoolean","SPLIT",EDGE,{"disambiguationData":[TD([subQ4])],"derivedFrom":makeQuery(id+"FMRX2liYoJm4zaX_1.6.F3.boolean.opBoolean","SPLIT",EDGE,{"disambiguationData":[TD([subQ4])],"derivedFrom":makeQuery(id+"FMRX2liYoJm4zaX_1.5.F3.boolean.opBoolean","SPLIT",EDGE,{"disambiguationData":[TD([subQ4])],"derivedFrom":makeQuery(id+"FMRX2liYoJm4zaX_1.4.F3.boolean.opBoolean","SPLIT",EDGE,{"disambiguationData":[TD([subQ4])],"derivedFrom":makeQuery(id+"FMRX2liYoJm4zaX_1.3.F3.boolean.opBoolean","SPLIT",EDGE,{"disambiguationData":[TD([subQ4])],"derivedFrom":makeQuery(id+"FMRX2liYoJm4zaX_1.2.F3.boolean.opBoolean","SPLIT",EDGE,{"disambiguationData":[TD([subQ4])],"derivedFrom":makeQuery(id+"FMRX2liYoJm4zaX_1.1.F3.boolean.opBoolean","SPLIT",EDGE,{"disambiguationData":[TD([subQ4])],"derivedFrom":makeQuery(id+"F1.opExtrude","CAP_EDGE",EDGE,{"disambiguationData":[OSD([subQ0])],"isStart":false})})})})})})})})})})})})})})})})})});}
            var Q1;
            Q1=makeQuery(id+"F3.boolean.opBoolean","COPY",EDGE,{"derivedFrom":makeQuery(id+"F3.opExtrude","SWEPT_EDGE",EDGE,{"disambiguationData":[OSD([sQuery(id+"F0.wireOp",EDGE,"E0"),sQuery(id+"F2.wireOp",EDGE,"E3"),sQuery(id+"F2.wireOp",EDGE,"E11.0")])]})});
            var Q2;
            Q2=makeQuery(id+"FMRX2liYoJm4zaX_1.17.F3.boolean.opBoolean","COPY",EDGE,{"derivedFrom":makeQuery(id+"FMRX2liYoJm4zaX_1.17.F3.opExtrude","SWEPT_EDGE",EDGE,{"disambiguationData":[OSD([sQuery(id+"F0.wireOp",EDGE,"E0"),sQuery(id+"F2.wireOp",EDGE,"E2"),sQuery(id+"F2.wireOp",EDGE,"E11.0")])]})});
            var Q3;
            Q3=makeQuery(id+"FMRX2liYoJm4zaX_1.17.F3.boolean.opBoolean","COPY",EDGE,{"derivedFrom":makeQuery(id+"FMRX2liYoJm4zaX_1.17.F3.opExtrude","SWEPT_EDGE",EDGE,{"disambiguationData":[OSD([sQuery(id+"F0.wireOp",EDGE,"E0"),sQuery(id+"F2.wireOp",EDGE,"E3"),sQuery(id+"F2.wireOp",EDGE,"E11.0")])]})});
            var Q4;
            {var subQ0=sQuery(id+"F0.wireOp",EDGE,"E0");var subQ3=sQuery(id+"F2.wireOp",EDGE,"E2");var subQ4=makeQuery(id+"FMRX2liYoJm4zaX_1.16.F3.opExtrude","SWEPT_FACE",FACE,{"disambiguationData":[OSD([subQ3])]});var subQ5=sQuery(id+"F2.wireOp",EDGE,"E3");var subQ6=makeQuery(id+"F3.boolean.opBoolean","COPY",FACE,{"derivedFrom":makeQuery(id+"F3.opExtrude","SWEPT_FACE",FACE,{"disambiguationData":[OSD([subQ5])]})});Q4=makeQuery(id+"FMRX2liYoJm4zaX_1.17.F3.boolean.opBoolean","SPLIT",EDGE,{"disambiguationData":[TD([makeQuery(id+"FMRX2liYoJm4zaX_1.16.F3.boolean.opBoolean","COPY",FACE,{"derivedFrom":subQ4})])],"derivedFrom":makeQuery(id+"FMRX2liYoJm4zaX_1.16.F3.boolean.opBoolean","SPLIT",EDGE,{"disambiguationData":[TD([subQ6])],"derivedFrom":makeQuery(id+"FMRX2liYoJm4zaX_1.15.F3.boolean.opBoolean","SPLIT",EDGE,{"disambiguationData":[TD([subQ6])],"derivedFrom":makeQuery(id+"FMRX2liYoJm4zaX_1.14.F3.boolean.opBoolean","SPLIT",EDGE,{"disambiguationData":[TD([subQ6])],"derivedFrom":makeQuery(id+"FMRX2liYoJm4zaX_1.13.F3.boolean.opBoolean","SPLIT",EDGE,{"disambiguationData":[TD([subQ6])],"derivedFrom":makeQuery(id+"FMRX2liYoJm4zaX_1.12.F3.boolean.opBoolean","SPLIT",EDGE,{"disambiguationData":[TD([subQ6])],"derivedFrom":makeQuery(id+"FMRX2liYoJm4zaX_1.11.F3.boolean.opBoolean","SPLIT",EDGE,{"disambiguationData":[TD([subQ6])],"derivedFrom":makeQuery(id+"FMRX2liYoJm4zaX_1.10.F3.boolean.opBoolean","SPLIT",EDGE,{"disambiguationData":[TD([subQ6])],"derivedFrom":makeQuery(id+"FMRX2liYoJm4zaX_1.9.F3.boolean.opBoolean","SPLIT",EDGE,{"disambiguationData":[TD([subQ6])],"derivedFrom":makeQuery(id+"FMRX2liYoJm4zaX_1.8.F3.boolean.opBoolean","SPLIT",EDGE,{"disambiguationData":[TD([subQ6])],"derivedFrom":makeQuery(id+"FMRX2liYoJm4zaX_1.7.F3.boolean.opBoolean","SPLIT",EDGE,{"disambiguationData":[TD([subQ6])],"derivedFrom":makeQuery(id+"FMRX2liYoJm4zaX_1.6.F3.boolean.opBoolean","SPLIT",EDGE,{"disambiguationData":[TD([subQ6])],"derivedFrom":makeQuery(id+"FMRX2liYoJm4zaX_1.5.F3.boolean.opBoolean","SPLIT",EDGE,{"disambiguationData":[TD([subQ6])],"derivedFrom":makeQuery(id+"FMRX2liYoJm4zaX_1.4.F3.boolean.opBoolean","SPLIT",EDGE,{"disambiguationData":[TD([subQ6])],"derivedFrom":makeQuery(id+"FMRX2liYoJm4zaX_1.3.F3.boolean.opBoolean","SPLIT",EDGE,{"disambiguationData":[TD([subQ6])],"derivedFrom":makeQuery(id+"FMRX2liYoJm4zaX_1.2.F3.boolean.opBoolean","SPLIT",EDGE,{"disambiguationData":[TD([subQ6])],"derivedFrom":makeQuery(id+"FMRX2liYoJm4zaX_1.1.F3.boolean.opBoolean","SPLIT",EDGE,{"disambiguationData":[TD([subQ6])],"derivedFrom":makeQuery(id+"F1.opExtrude","CAP_EDGE",EDGE,{"disambiguationData":[OSD([subQ0])],"isStart":false})})})})})})})})})})})})})})})})})});}
            var Q5;
            Q5=makeQuery(id+"FMRX2liYoJm4zaX_1.16.F3.boolean.opBoolean","COPY",EDGE,{"derivedFrom":makeQuery(id+"FMRX2liYoJm4zaX_1.16.F3.opExtrude","SWEPT_EDGE",EDGE,{"disambiguationData":[OSD([sQuery(id+"F0.wireOp",EDGE,"E0"),sQuery(id+"F2.wireOp",EDGE,"E2"),sQuery(id+"F2.wireOp",EDGE,"E11.0")])]})});
            var Q6;
            Q6=makeQuery(id+"FMRX2liYoJm4zaX_1.17.F3.boolean.opBoolean","COPY",EDGE,{"derivedFrom":makeQuery(id+"FMRX2liYoJm4zaX_1.17.F3.opExtrude","CAP_EDGE",EDGE,{"disambiguationData":[OSD([sQuery(id+"F2.wireOp",EDGE,"E2")])],"isStart":true})});
            var Q7;
            Q7=makeQuery(id+"FMRX2liYoJm4zaX_1.17.F3.boolean.opBoolean","COPY",EDGE,{"derivedFrom":makeQuery(id+"FMRX2liYoJm4zaX_1.17.F3.opExtrude","CAP_EDGE",EDGE,{"disambiguationData":[OSD([sQuery(id+"F2.wireOp",EDGE,"E10")])],"isStart":true})});
            var Q8;
            Q8=makeQuery(id+"FMRX2liYoJm4zaX_1.17.F3.boolean.opBoolean","COPY",EDGE,{"derivedFrom":makeQuery(id+"FMRX2liYoJm4zaX_1.17.F3.opExtrude","CAP_EDGE",EDGE,{"disambiguationData":[OSD([sQuery(id+"F2.wireOp",EDGE,"E3")])],"isStart":true})});
            var Q9;
            Q9=makeQuery(id+"FMRX2liYoJm4zaX_1.16.F3.boolean.opBoolean","COPY",EDGE,{"derivedFrom":makeQuery(id+"FMRX2liYoJm4zaX_1.16.F3.opExtrude","CAP_EDGE",EDGE,{"disambiguationData":[OSD([sQuery(id+"F2.wireOp",EDGE,"E2")])],"isStart":true})});
            var Q10;
            Q10=makeQuery(id+"FMRX2liYoJm4zaX_1.16.F3.boolean.opBoolean","COPY",EDGE,{"derivedFrom":makeQuery(id+"FMRX2liYoJm4zaX_1.16.F3.opExtrude","CAP_EDGE",EDGE,{"disambiguationData":[OSD([sQuery(id+"F2.wireOp",EDGE,"E10")])],"isStart":true})});
            var Q11;
            Q11=makeQuery(id+"FMRX2liYoJm4zaX_1.16.F3.boolean.opBoolean","COPY",EDGE,{"derivedFrom":makeQuery(id+"FMRX2liYoJm4zaX_1.16.F3.opExtrude","CAP_EDGE",EDGE,{"disambiguationData":[OSD([sQuery(id+"F2.wireOp",EDGE,"E3")])],"isStart":true})});
            var Q12;
            Q12=makeQuery(id+"FMRX2liYoJm4zaX_1.16.F3.boolean.opBoolean","COPY",EDGE,{"derivedFrom":makeQuery(id+"FMRX2liYoJm4zaX_1.16.F3.opExtrude","SWEPT_EDGE",EDGE,{"disambiguationData":[OSD([sQuery(id+"F0.wireOp",EDGE,"E0"),sQuery(id+"F2.wireOp",EDGE,"E3"),sQuery(id+"F2.wireOp",EDGE,"E11.0")])]})});
            var Q13;
            {var subQ0=sQuery(id+"F0.wireOp",EDGE,"E0");var subQ2=sQuery(id+"F2.wireOp",EDGE,"E3");var subQ4=sQuery(id+"F2.wireOp",EDGE,"E2");var subQ5=makeQuery(id+"FMRX2liYoJm4zaX_1.15.F3.opExtrude","SWEPT_FACE",FACE,{"disambiguationData":[OSD([subQ4])]});var subQ6=makeQuery(id+"F3.boolean.opBoolean","COPY",FACE,{"derivedFrom":makeQuery(id+"F3.opExtrude","SWEPT_FACE",FACE,{"disambiguationData":[OSD([subQ2])]})});Q13=makeQuery(id+"FMRX2liYoJm4zaX_1.16.F3.boolean.opBoolean","SPLIT",EDGE,{"disambiguationData":[TD([makeQuery(id+"FMRX2liYoJm4zaX_1.15.F3.boolean.opBoolean","COPY",FACE,{"derivedFrom":subQ5})])],"derivedFrom":makeQuery(id+"FMRX2liYoJm4zaX_1.15.F3.boolean.opBoolean","SPLIT",EDGE,{"disambiguationData":[TD([subQ6])],"derivedFrom":makeQuery(id+"FMRX2liYoJm4zaX_1.14.F3.boolean.opBoolean","SPLIT",EDGE,{"disambiguationData":[TD([subQ6])],"derivedFrom":makeQuery(id+"FMRX2liYoJm4zaX_1.13.F3.boolean.opBoolean","SPLIT",EDGE,{"disambiguationData":[TD([subQ6])],"derivedFrom":makeQuery(id+"FMRX2liYoJm4zaX_1.12.F3.boolean.opBoolean","SPLIT",EDGE,{"disambiguationData":[TD([subQ6])],"derivedFrom":makeQuery(id+"FMRX2liYoJm4zaX_1.11.F3.boolean.opBoolean","SPLIT",EDGE,{"disambiguationData":[TD([subQ6])],"derivedFrom":makeQuery(id+"FMRX2liYoJm4zaX_1.10.F3.boolean.opBoolean","SPLIT",EDGE,{"disambiguationData":[TD([subQ6])],"derivedFrom":makeQuery(id+"FMRX2liYoJm4zaX_1.9.F3.boolean.opBoolean","SPLIT",EDGE,{"disambiguationData":[TD([subQ6])],"derivedFrom":makeQuery(id+"FMRX2liYoJm4zaX_1.8.F3.boolean.opBoolean","SPLIT",EDGE,{"disambiguationData":[TD([subQ6])],"derivedFrom":makeQuery(id+"FMRX2liYoJm4zaX_1.7.F3.boolean.opBoolean","SPLIT",EDGE,{"disambiguationData":[TD([subQ6])],"derivedFrom":makeQuery(id+"FMRX2liYoJm4zaX_1.6.F3.boolean.opBoolean","SPLIT",EDGE,{"disambiguationData":[TD([subQ6])],"derivedFrom":makeQuery(id+"FMRX2liYoJm4zaX_1.5.F3.boolean.opBoolean","SPLIT",EDGE,{"disambiguationData":[TD([subQ6])],"derivedFrom":makeQuery(id+"FMRX2liYoJm4zaX_1.4.F3.boolean.opBoolean","SPLIT",EDGE,{"disambiguationData":[TD([subQ6])],"derivedFrom":makeQuery(id+"FMRX2liYoJm4zaX_1.3.F3.boolean.opBoolean","SPLIT",EDGE,{"disambiguationData":[TD([subQ6])],"derivedFrom":makeQuery(id+"FMRX2liYoJm4zaX_1.2.F3.boolean.opBoolean","SPLIT",EDGE,{"disambiguationData":[TD([subQ6])],"derivedFrom":makeQuery(id+"FMRX2liYoJm4zaX_1.1.F3.boolean.opBoolean","SPLIT",EDGE,{"disambiguationData":[TD([subQ6])],"derivedFrom":makeQuery(id+"F1.opExtrude","CAP_EDGE",EDGE,{"disambiguationData":[OSD([subQ0])],"isStart":false})})})})})})})})})})})})})})})})});}
            var Q14;
            Q14=makeQuery(id+"FMRX2liYoJm4zaX_1.15.F3.boolean.opBoolean","COPY",EDGE,{"derivedFrom":makeQuery(id+"FMRX2liYoJm4zaX_1.15.F3.opExtrude","SWEPT_EDGE",EDGE,{"disambiguationData":[OSD([sQuery(id+"F0.wireOp",EDGE,"E0"),sQuery(id+"F2.wireOp",EDGE,"E2"),sQuery(id+"F2.wireOp",EDGE,"E11.0")])]})});
            var Q15;
            Q15=makeQuery(id+"FMRX2liYoJm4zaX_1.15.F3.boolean.opBoolean","COPY",EDGE,{"derivedFrom":makeQuery(id+"FMRX2liYoJm4zaX_1.15.F3.opExtrude","CAP_EDGE",EDGE,{"disambiguationData":[OSD([sQuery(id+"F2.wireOp",EDGE,"E2")])],"isStart":true})});
            var Q16;
            Q16=makeQuery(id+"FMRX2liYoJm4zaX_1.15.F3.boolean.opBoolean","COPY",EDGE,{"derivedFrom":makeQuery(id+"FMRX2liYoJm4zaX_1.15.F3.opExtrude","CAP_EDGE",EDGE,{"disambiguationData":[OSD([sQuery(id+"F2.wireOp",EDGE,"E10")])],"isStart":true})});
            var Q17;
            Q17=makeQuery(id+"FMRX2liYoJm4zaX_1.15.F3.boolean.opBoolean","COPY",EDGE,{"derivedFrom":makeQuery(id+"FMRX2liYoJm4zaX_1.15.F3.opExtrude","CAP_EDGE",EDGE,{"disambiguationData":[OSD([sQuery(id+"F2.wireOp",EDGE,"E3")])],"isStart":true})});
            var Q18;
            Q18=makeQuery(id+"FMRX2liYoJm4zaX_1.15.F3.boolean.opBoolean","COPY",EDGE,{"derivedFrom":makeQuery(id+"FMRX2liYoJm4zaX_1.15.F3.opExtrude","SWEPT_EDGE",EDGE,{"disambiguationData":[OSD([sQuery(id+"F0.wireOp",EDGE,"E0"),sQuery(id+"F2.wireOp",EDGE,"E3"),sQuery(id+"F2.wireOp",EDGE,"E11.0")])]})});
            var Q19;
            {var subQ0=sQuery(id+"F0.wireOp",EDGE,"E0");var subQ3=sQuery(id+"F2.wireOp",EDGE,"E2");var subQ4=makeQuery(id+"FMRX2liYoJm4zaX_1.14.F3.opExtrude","SWEPT_FACE",FACE,{"disambiguationData":[OSD([subQ3])]});var subQ5=sQuery(id+"F2.wireOp",EDGE,"E3");var subQ6=makeQuery(id+"F3.boolean.opBoolean","COPY",FACE,{"derivedFrom":makeQuery(id+"F3.opExtrude","SWEPT_FACE",FACE,{"disambiguationData":[OSD([subQ5])]})});Q19=makeQuery(id+"FMRX2liYoJm4zaX_1.15.F3.boolean.opBoolean","SPLIT",EDGE,{"disambiguationData":[TD([makeQuery(id+"FMRX2liYoJm4zaX_1.14.F3.boolean.opBoolean","COPY",FACE,{"derivedFrom":subQ4})])],"derivedFrom":makeQuery(id+"FMRX2liYoJm4zaX_1.14.F3.boolean.opBoolean","SPLIT",EDGE,{"disambiguationData":[TD([subQ6])],"derivedFrom":makeQuery(id+"FMRX2liYoJm4zaX_1.13.F3.boolean.opBoolean","SPLIT",EDGE,{"disambiguationData":[TD([subQ6])],"derivedFrom":makeQuery(id+"FMRX2liYoJm4zaX_1.12.F3.boolean.opBoolean","SPLIT",EDGE,{"disambiguationData":[TD([subQ6])],"derivedFrom":makeQuery(id+"FMRX2liYoJm4zaX_1.11.F3.boolean.opBoolean","SPLIT",EDGE,{"disambiguationData":[TD([subQ6])],"derivedFrom":makeQuery(id+"FMRX2liYoJm4zaX_1.10.F3.boolean.opBoolean","SPLIT",EDGE,{"disambiguationData":[TD([subQ6])],"derivedFrom":makeQuery(id+"FMRX2liYoJm4zaX_1.9.F3.boolean.opBoolean","SPLIT",EDGE,{"disambiguationData":[TD([subQ6])],"derivedFrom":makeQuery(id+"FMRX2liYoJm4zaX_1.8.F3.boolean.opBoolean","SPLIT",EDGE,{"disambiguationData":[TD([subQ6])],"derivedFrom":makeQuery(id+"FMRX2liYoJm4zaX_1.7.F3.boolean.opBoolean","SPLIT",EDGE,{"disambiguationData":[TD([subQ6])],"derivedFrom":makeQuery(id+"FMRX2liYoJm4zaX_1.6.F3.boolean.opBoolean","SPLIT",EDGE,{"disambiguationData":[TD([subQ6])],"derivedFrom":makeQuery(id+"FMRX2liYoJm4zaX_1.5.F3.boolean.opBoolean","SPLIT",EDGE,{"disambiguationData":[TD([subQ6])],"derivedFrom":makeQuery(id+"FMRX2liYoJm4zaX_1.4.F3.boolean.opBoolean","SPLIT",EDGE,{"disambiguationData":[TD([subQ6])],"derivedFrom":makeQuery(id+"FMRX2liYoJm4zaX_1.3.F3.boolean.opBoolean","SPLIT",EDGE,{"disambiguationData":[TD([subQ6])],"derivedFrom":makeQuery(id+"FMRX2liYoJm4zaX_1.2.F3.boolean.opBoolean","SPLIT",EDGE,{"disambiguationData":[TD([subQ6])],"derivedFrom":makeQuery(id+"FMRX2liYoJm4zaX_1.1.F3.boolean.opBoolean","SPLIT",EDGE,{"disambiguationData":[TD([subQ6])],"derivedFrom":makeQuery(id+"F1.opExtrude","CAP_EDGE",EDGE,{"disambiguationData":[OSD([subQ0])],"isStart":false})})})})})})})})})})})})})})})});}
            var Q20;
            Q20=makeQuery(id+"FMRX2liYoJm4zaX_1.14.F3.boolean.opBoolean","COPY",EDGE,{"derivedFrom":makeQuery(id+"FMRX2liYoJm4zaX_1.14.F3.opExtrude","SWEPT_EDGE",EDGE,{"disambiguationData":[OSD([sQuery(id+"F0.wireOp",EDGE,"E0"),sQuery(id+"F2.wireOp",EDGE,"E2"),sQuery(id+"F2.wireOp",EDGE,"E11.0")])]})});
            var Q21;
            Q21=makeQuery(id+"FMRX2liYoJm4zaX_1.14.F3.boolean.opBoolean","COPY",EDGE,{"derivedFrom":makeQuery(id+"FMRX2liYoJm4zaX_1.14.F3.opExtrude","CAP_EDGE",EDGE,{"disambiguationData":[OSD([sQuery(id+"F2.wireOp",EDGE,"E2")])],"isStart":true})});
            var Q22;
            Q22=makeQuery(id+"FMRX2liYoJm4zaX_1.14.F3.boolean.opBoolean","COPY",EDGE,{"derivedFrom":makeQuery(id+"FMRX2liYoJm4zaX_1.14.F3.opExtrude","CAP_EDGE",EDGE,{"disambiguationData":[OSD([sQuery(id+"F2.wireOp",EDGE,"E10")])],"isStart":true})});
            var Q23;
            Q23=makeQuery(id+"FMRX2liYoJm4zaX_1.14.F3.boolean.opBoolean","COPY",EDGE,{"derivedFrom":makeQuery(id+"FMRX2liYoJm4zaX_1.14.F3.opExtrude","CAP_EDGE",EDGE,{"disambiguationData":[OSD([sQuery(id+"F2.wireOp",EDGE,"E3")])],"isStart":true})});
            var Q24;
            Q24=makeQuery(id+"FMRX2liYoJm4zaX_1.14.F3.boolean.opBoolean","COPY",EDGE,{"derivedFrom":makeQuery(id+"FMRX2liYoJm4zaX_1.14.F3.opExtrude","SWEPT_EDGE",EDGE,{"disambiguationData":[OSD([sQuery(id+"F0.wireOp",EDGE,"E0"),sQuery(id+"F2.wireOp",EDGE,"E3"),sQuery(id+"F2.wireOp",EDGE,"E11.0")])]})});
            var Q25;
            {var subQ0=sQuery(id+"F0.wireOp",EDGE,"E0");var subQ3=sQuery(id+"F2.wireOp",EDGE,"E2");var subQ4=makeQuery(id+"FMRX2liYoJm4zaX_1.13.F3.opExtrude","SWEPT_FACE",FACE,{"disambiguationData":[OSD([subQ3])]});var subQ5=sQuery(id+"F2.wireOp",EDGE,"E3");var subQ6=makeQuery(id+"F3.boolean.opBoolean","COPY",FACE,{"derivedFrom":makeQuery(id+"F3.opExtrude","SWEPT_FACE",FACE,{"disambiguationData":[OSD([subQ5])]})});Q25=makeQuery(id+"FMRX2liYoJm4zaX_1.14.F3.boolean.opBoolean","SPLIT",EDGE,{"disambiguationData":[TD([makeQuery(id+"FMRX2liYoJm4zaX_1.13.F3.boolean.opBoolean","COPY",FACE,{"derivedFrom":subQ4})])],"derivedFrom":makeQuery(id+"FMRX2liYoJm4zaX_1.13.F3.boolean.opBoolean","SPLIT",EDGE,{"disambiguationData":[TD([subQ6])],"derivedFrom":makeQuery(id+"FMRX2liYoJm4zaX_1.12.F3.boolean.opBoolean","SPLIT",EDGE,{"disambiguationData":[TD([subQ6])],"derivedFrom":makeQuery(id+"FMRX2liYoJm4zaX_1.11.F3.boolean.opBoolean","SPLIT",EDGE,{"disambiguationData":[TD([subQ6])],"derivedFrom":makeQuery(id+"FMRX2liYoJm4zaX_1.10.F3.boolean.opBoolean","SPLIT",EDGE,{"disambiguationData":[TD([subQ6])],"derivedFrom":makeQuery(id+"FMRX2liYoJm4zaX_1.9.F3.boolean.opBoolean","SPLIT",EDGE,{"disambiguationData":[TD([subQ6])],"derivedFrom":makeQuery(id+"FMRX2liYoJm4zaX_1.8.F3.boolean.opBoolean","SPLIT",EDGE,{"disambiguationData":[TD([subQ6])],"derivedFrom":makeQuery(id+"FMRX2liYoJm4zaX_1.7.F3.boolean.opBoolean","SPLIT",EDGE,{"disambiguationData":[TD([subQ6])],"derivedFrom":makeQuery(id+"FMRX2liYoJm4zaX_1.6.F3.boolean.opBoolean","SPLIT",EDGE,{"disambiguationData":[TD([subQ6])],"derivedFrom":makeQuery(id+"FMRX2liYoJm4zaX_1.5.F3.boolean.opBoolean","SPLIT",EDGE,{"disambiguationData":[TD([subQ6])],"derivedFrom":makeQuery(id+"FMRX2liYoJm4zaX_1.4.F3.boolean.opBoolean","SPLIT",EDGE,{"disambiguationData":[TD([subQ6])],"derivedFrom":makeQuery(id+"FMRX2liYoJm4zaX_1.3.F3.boolean.opBoolean","SPLIT",EDGE,{"disambiguationData":[TD([subQ6])],"derivedFrom":makeQuery(id+"FMRX2liYoJm4zaX_1.2.F3.boolean.opBoolean","SPLIT",EDGE,{"disambiguationData":[TD([subQ6])],"derivedFrom":makeQuery(id+"FMRX2liYoJm4zaX_1.1.F3.boolean.opBoolean","SPLIT",EDGE,{"disambiguationData":[TD([subQ6])],"derivedFrom":makeQuery(id+"F1.opExtrude","CAP_EDGE",EDGE,{"disambiguationData":[OSD([subQ0])],"isStart":false})})})})})})})})})})})})})})});}
            var Q26;
            Q26=makeQuery(id+"FMRX2liYoJm4zaX_1.13.F3.boolean.opBoolean","COPY",EDGE,{"derivedFrom":makeQuery(id+"FMRX2liYoJm4zaX_1.13.F3.opExtrude","SWEPT_EDGE",EDGE,{"disambiguationData":[OSD([sQuery(id+"F0.wireOp",EDGE,"E0"),sQuery(id+"F2.wireOp",EDGE,"E2"),sQuery(id+"F2.wireOp",EDGE,"E11.0")])]})});
            var Q27;
            Q27=makeQuery(id+"FMRX2liYoJm4zaX_1.13.F3.boolean.opBoolean","COPY",EDGE,{"derivedFrom":makeQuery(id+"FMRX2liYoJm4zaX_1.13.F3.opExtrude","CAP_EDGE",EDGE,{"disambiguationData":[OSD([sQuery(id+"F2.wireOp",EDGE,"E2")])],"isStart":true})});
            var Q28;
            Q28=makeQuery(id+"FMRX2liYoJm4zaX_1.13.F3.boolean.opBoolean","COPY",EDGE,{"derivedFrom":makeQuery(id+"FMRX2liYoJm4zaX_1.13.F3.opExtrude","CAP_EDGE",EDGE,{"disambiguationData":[OSD([sQuery(id+"F2.wireOp",EDGE,"E10")])],"isStart":true})});
            var Q29;
            Q29=makeQuery(id+"FMRX2liYoJm4zaX_1.13.F3.boolean.opBoolean","COPY",EDGE,{"derivedFrom":makeQuery(id+"FMRX2liYoJm4zaX_1.13.F3.opExtrude","SWEPT_EDGE",EDGE,{"disambiguationData":[OSD([sQuery(id+"F0.wireOp",EDGE,"E0"),sQuery(id+"F2.wireOp",EDGE,"E3"),sQuery(id+"F2.wireOp",EDGE,"E11.0")])]})});
            var Q30;
            Q30=makeQuery(id+"FMRX2liYoJm4zaX_1.13.F3.boolean.opBoolean","COPY",EDGE,{"derivedFrom":makeQuery(id+"FMRX2liYoJm4zaX_1.13.F3.opExtrude","CAP_EDGE",EDGE,{"disambiguationData":[OSD([sQuery(id+"F2.wireOp",EDGE,"E3")])],"isStart":true})});
            var Q31;
            Q31=makeQuery(id+"FMRX2liYoJm4zaX_1.12.F3.boolean.opBoolean","COPY",EDGE,{"derivedFrom":makeQuery(id+"FMRX2liYoJm4zaX_1.12.F3.opExtrude","CAP_EDGE",EDGE,{"disambiguationData":[OSD([sQuery(id+"F2.wireOp",EDGE,"E2")])],"isStart":true})});
            var Q32;
            Q32=makeQuery(id+"FMRX2liYoJm4zaX_1.12.F3.boolean.opBoolean","COPY",EDGE,{"derivedFrom":makeQuery(id+"FMRX2liYoJm4zaX_1.12.F3.opExtrude","SWEPT_EDGE",EDGE,{"disambiguationData":[OSD([sQuery(id+"F0.wireOp",EDGE,"E0"),sQuery(id+"F2.wireOp",EDGE,"E2"),sQuery(id+"F2.wireOp",EDGE,"E11.0")])]})});
            var Q33;
            Q33=makeQuery(id+"FMRX2liYoJm4zaX_1.12.F3.boolean.opBoolean","COPY",EDGE,{"derivedFrom":makeQuery(id+"FMRX2liYoJm4zaX_1.12.F3.opExtrude","CAP_EDGE",EDGE,{"disambiguationData":[OSD([sQuery(id+"F2.wireOp",EDGE,"E10")])],"isStart":true})});
            var Q34;
            Q34=makeQuery(id+"FMRX2liYoJm4zaX_1.12.F3.boolean.opBoolean","COPY",EDGE,{"derivedFrom":makeQuery(id+"FMRX2liYoJm4zaX_1.12.F3.opExtrude","CAP_EDGE",EDGE,{"disambiguationData":[OSD([sQuery(id+"F2.wireOp",EDGE,"E3")])],"isStart":true})});
            var Q35;
            Q35=makeQuery(id+"FMRX2liYoJm4zaX_1.12.F3.boolean.opBoolean","COPY",EDGE,{"derivedFrom":makeQuery(id+"FMRX2liYoJm4zaX_1.12.F3.opExtrude","SWEPT_EDGE",EDGE,{"disambiguationData":[OSD([sQuery(id+"F0.wireOp",EDGE,"E0"),sQuery(id+"F2.wireOp",EDGE,"E3"),sQuery(id+"F2.wireOp",EDGE,"E11.0")])]})});
            var Q36;
            Q36=makeQuery(id+"FMRX2liYoJm4zaX_1.11.F3.boolean.opBoolean","COPY",EDGE,{"derivedFrom":makeQuery(id+"FMRX2liYoJm4zaX_1.11.F3.opExtrude","SWEPT_EDGE",EDGE,{"disambiguationData":[OSD([sQuery(id+"F0.wireOp",EDGE,"E0"),sQuery(id+"F2.wireOp",EDGE,"E2"),sQuery(id+"F2.wireOp",EDGE,"E11.0")])]})});
            var Q37;
            {var subQ0=sQuery(id+"F0.wireOp",EDGE,"E0");var subQ3=sQuery(id+"F2.wireOp",EDGE,"E2");var subQ4=makeQuery(id+"FMRX2liYoJm4zaX_1.11.F3.opExtrude","SWEPT_FACE",FACE,{"disambiguationData":[OSD([subQ3])]});var subQ5=sQuery(id+"F2.wireOp",EDGE,"E3");var subQ6=makeQuery(id+"F3.boolean.opBoolean","COPY",FACE,{"derivedFrom":makeQuery(id+"F3.opExtrude","SWEPT_FACE",FACE,{"disambiguationData":[OSD([subQ5])]})});Q37=makeQuery(id+"FMRX2liYoJm4zaX_1.12.F3.boolean.opBoolean","SPLIT",EDGE,{"disambiguationData":[TD([makeQuery(id+"FMRX2liYoJm4zaX_1.11.F3.boolean.opBoolean","COPY",FACE,{"derivedFrom":subQ4})])],"derivedFrom":makeQuery(id+"FMRX2liYoJm4zaX_1.11.F3.boolean.opBoolean","SPLIT",EDGE,{"disambiguationData":[TD([subQ6])],"derivedFrom":makeQuery(id+"FMRX2liYoJm4zaX_1.10.F3.boolean.opBoolean","SPLIT",EDGE,{"disambiguationData":[TD([subQ6])],"derivedFrom":makeQuery(id+"FMRX2liYoJm4zaX_1.9.F3.boolean.opBoolean","SPLIT",EDGE,{"disambiguationData":[TD([subQ6])],"derivedFrom":makeQuery(id+"FMRX2liYoJm4zaX_1.8.F3.boolean.opBoolean","SPLIT",EDGE,{"disambiguationData":[TD([subQ6])],"derivedFrom":makeQuery(id+"FMRX2liYoJm4zaX_1.7.F3.boolean.opBoolean","SPLIT",EDGE,{"disambiguationData":[TD([subQ6])],"derivedFrom":makeQuery(id+"FMRX2liYoJm4zaX_1.6.F3.boolean.opBoolean","SPLIT",EDGE,{"disambiguationData":[TD([subQ6])],"derivedFrom":makeQuery(id+"FMRX2liYoJm4zaX_1.5.F3.boolean.opBoolean","SPLIT",EDGE,{"disambiguationData":[TD([subQ6])],"derivedFrom":makeQuery(id+"FMRX2liYoJm4zaX_1.4.F3.boolean.opBoolean","SPLIT",EDGE,{"disambiguationData":[TD([subQ6])],"derivedFrom":makeQuery(id+"FMRX2liYoJm4zaX_1.3.F3.boolean.opBoolean","SPLIT",EDGE,{"disambiguationData":[TD([subQ6])],"derivedFrom":makeQuery(id+"FMRX2liYoJm4zaX_1.2.F3.boolean.opBoolean","SPLIT",EDGE,{"disambiguationData":[TD([subQ6])],"derivedFrom":makeQuery(id+"FMRX2liYoJm4zaX_1.1.F3.boolean.opBoolean","SPLIT",EDGE,{"disambiguationData":[TD([subQ6])],"derivedFrom":makeQuery(id+"F1.opExtrude","CAP_EDGE",EDGE,{"disambiguationData":[OSD([subQ0])],"isStart":false})})})})})})})})})})})})});}
            var Q38;
            Q38=makeQuery(id+"FMRX2liYoJm4zaX_1.11.F3.boolean.opBoolean","COPY",EDGE,{"derivedFrom":makeQuery(id+"FMRX2liYoJm4zaX_1.11.F3.opExtrude","CAP_EDGE",EDGE,{"disambiguationData":[OSD([sQuery(id+"F2.wireOp",EDGE,"E2")])],"isStart":true})});
            var Q39;
            Q39=makeQuery(id+"FMRX2liYoJm4zaX_1.11.F3.boolean.opBoolean","COPY",EDGE,{"derivedFrom":makeQuery(id+"FMRX2liYoJm4zaX_1.11.F3.opExtrude","CAP_EDGE",EDGE,{"disambiguationData":[OSD([sQuery(id+"F2.wireOp",EDGE,"E10")])],"isStart":true})});
            var Q40;
            Q40=makeQuery(id+"FMRX2liYoJm4zaX_1.11.F3.boolean.opBoolean","COPY",EDGE,{"derivedFrom":makeQuery(id+"FMRX2liYoJm4zaX_1.11.F3.opExtrude","CAP_EDGE",EDGE,{"disambiguationData":[OSD([sQuery(id+"F2.wireOp",EDGE,"E3")])],"isStart":true})});
            var Q41;
            Q41=makeQuery(id+"FMRX2liYoJm4zaX_1.11.F3.boolean.opBoolean","COPY",EDGE,{"derivedFrom":makeQuery(id+"FMRX2liYoJm4zaX_1.11.F3.opExtrude","SWEPT_EDGE",EDGE,{"disambiguationData":[OSD([sQuery(id+"F0.wireOp",EDGE,"E0"),sQuery(id+"F2.wireOp",EDGE,"E3"),sQuery(id+"F2.wireOp",EDGE,"E11.0")])]})});
            var Q42;
            {var subQ0=sQuery(id+"F0.wireOp",EDGE,"E0");var subQ3=sQuery(id+"F2.wireOp",EDGE,"E2");var subQ4=makeQuery(id+"FMRX2liYoJm4zaX_1.10.F3.opExtrude","SWEPT_FACE",FACE,{"disambiguationData":[OSD([subQ3])]});var subQ5=sQuery(id+"F2.wireOp",EDGE,"E3");var subQ6=makeQuery(id+"F3.boolean.opBoolean","COPY",FACE,{"derivedFrom":makeQuery(id+"F3.opExtrude","SWEPT_FACE",FACE,{"disambiguationData":[OSD([subQ5])]})});Q42=makeQuery(id+"FMRX2liYoJm4zaX_1.11.F3.boolean.opBoolean","SPLIT",EDGE,{"disambiguationData":[TD([makeQuery(id+"FMRX2liYoJm4zaX_1.10.F3.boolean.opBoolean","COPY",FACE,{"derivedFrom":subQ4})])],"derivedFrom":makeQuery(id+"FMRX2liYoJm4zaX_1.10.F3.boolean.opBoolean","SPLIT",EDGE,{"disambiguationData":[TD([subQ6])],"derivedFrom":makeQuery(id+"FMRX2liYoJm4zaX_1.9.F3.boolean.opBoolean","SPLIT",EDGE,{"disambiguationData":[TD([subQ6])],"derivedFrom":makeQuery(id+"FMRX2liYoJm4zaX_1.8.F3.boolean.opBoolean","SPLIT",EDGE,{"disambiguationData":[TD([subQ6])],"derivedFrom":makeQuery(id+"FMRX2liYoJm4zaX_1.7.F3.boolean.opBoolean","SPLIT",EDGE,{"disambiguationData":[TD([subQ6])],"derivedFrom":makeQuery(id+"FMRX2liYoJm4zaX_1.6.F3.boolean.opBoolean","SPLIT",EDGE,{"disambiguationData":[TD([subQ6])],"derivedFrom":makeQuery(id+"FMRX2liYoJm4zaX_1.5.F3.boolean.opBoolean","SPLIT",EDGE,{"disambiguationData":[TD([subQ6])],"derivedFrom":makeQuery(id+"FMRX2liYoJm4zaX_1.4.F3.boolean.opBoolean","SPLIT",EDGE,{"disambiguationData":[TD([subQ6])],"derivedFrom":makeQuery(id+"FMRX2liYoJm4zaX_1.3.F3.boolean.opBoolean","SPLIT",EDGE,{"disambiguationData":[TD([subQ6])],"derivedFrom":makeQuery(id+"FMRX2liYoJm4zaX_1.2.F3.boolean.opBoolean","SPLIT",EDGE,{"disambiguationData":[TD([subQ6])],"derivedFrom":makeQuery(id+"FMRX2liYoJm4zaX_1.1.F3.boolean.opBoolean","SPLIT",EDGE,{"disambiguationData":[TD([subQ6])],"derivedFrom":makeQuery(id+"F1.opExtrude","CAP_EDGE",EDGE,{"disambiguationData":[OSD([subQ0])],"isStart":false})})})})})})})})})})})});}
            var Q43;
            Q43=makeQuery(id+"FMRX2liYoJm4zaX_1.10.F3.boolean.opBoolean","COPY",EDGE,{"derivedFrom":makeQuery(id+"FMRX2liYoJm4zaX_1.10.F3.opExtrude","SWEPT_EDGE",EDGE,{"disambiguationData":[OSD([sQuery(id+"F0.wireOp",EDGE,"E0"),sQuery(id+"F2.wireOp",EDGE,"E2"),sQuery(id+"F2.wireOp",EDGE,"E11.0")])]})});
            var Q44;
            Q44=makeQuery(id+"FMRX2liYoJm4zaX_1.10.F3.boolean.opBoolean","COPY",EDGE,{"derivedFrom":makeQuery(id+"FMRX2liYoJm4zaX_1.10.F3.opExtrude","CAP_EDGE",EDGE,{"disambiguationData":[OSD([sQuery(id+"F2.wireOp",EDGE,"E2")])],"isStart":true})});
            var Q45;
            Q45=makeQuery(id+"FMRX2liYoJm4zaX_1.10.F3.boolean.opBoolean","COPY",EDGE,{"derivedFrom":makeQuery(id+"FMRX2liYoJm4zaX_1.10.F3.opExtrude","CAP_EDGE",EDGE,{"disambiguationData":[OSD([sQuery(id+"F2.wireOp",EDGE,"E10")])],"isStart":true})});
            var Q46;
            Q46=makeQuery(id+"FMRX2liYoJm4zaX_1.10.F3.boolean.opBoolean","COPY",EDGE,{"derivedFrom":makeQuery(id+"FMRX2liYoJm4zaX_1.10.F3.opExtrude","CAP_EDGE",EDGE,{"disambiguationData":[OSD([sQuery(id+"F2.wireOp",EDGE,"E3")])],"isStart":true})});
            var Q47;
            Q47=makeQuery(id+"FMRX2liYoJm4zaX_1.10.F3.boolean.opBoolean","COPY",EDGE,{"derivedFrom":makeQuery(id+"FMRX2liYoJm4zaX_1.10.F3.opExtrude","SWEPT_EDGE",EDGE,{"disambiguationData":[OSD([sQuery(id+"F0.wireOp",EDGE,"E0"),sQuery(id+"F2.wireOp",EDGE,"E3"),sQuery(id+"F2.wireOp",EDGE,"E11.0")])]})});
            var Q48;
            {var subQ0=sQuery(id+"F0.wireOp",EDGE,"E0");var subQ3=sQuery(id+"F2.wireOp",EDGE,"E3");var subQ4=sQuery(id+"F2.wireOp",EDGE,"E2");var subQ5=makeQuery(id+"FMRX2liYoJm4zaX_1.9.F3.opExtrude","SWEPT_FACE",FACE,{"disambiguationData":[OSD([subQ4])]});var subQ6=makeQuery(id+"F3.boolean.opBoolean","COPY",FACE,{"derivedFrom":makeQuery(id+"F3.opExtrude","SWEPT_FACE",FACE,{"disambiguationData":[OSD([subQ3])]})});Q48=makeQuery(id+"FMRX2liYoJm4zaX_1.10.F3.boolean.opBoolean","SPLIT",EDGE,{"disambiguationData":[TD([makeQuery(id+"FMRX2liYoJm4zaX_1.9.F3.boolean.opBoolean","COPY",FACE,{"derivedFrom":subQ5})])],"derivedFrom":makeQuery(id+"FMRX2liYoJm4zaX_1.9.F3.boolean.opBoolean","SPLIT",EDGE,{"disambiguationData":[TD([subQ6])],"derivedFrom":makeQuery(id+"FMRX2liYoJm4zaX_1.8.F3.boolean.opBoolean","SPLIT",EDGE,{"disambiguationData":[TD([subQ6])],"derivedFrom":makeQuery(id+"FMRX2liYoJm4zaX_1.7.F3.boolean.opBoolean","SPLIT",EDGE,{"disambiguationData":[TD([subQ6])],"derivedFrom":makeQuery(id+"FMRX2liYoJm4zaX_1.6.F3.boolean.opBoolean","SPLIT",EDGE,{"disambiguationData":[TD([subQ6])],"derivedFrom":makeQuery(id+"FMRX2liYoJm4zaX_1.5.F3.boolean.opBoolean","SPLIT",EDGE,{"disambiguationData":[TD([subQ6])],"derivedFrom":makeQuery(id+"FMRX2liYoJm4zaX_1.4.F3.boolean.opBoolean","SPLIT",EDGE,{"disambiguationData":[TD([subQ6])],"derivedFrom":makeQuery(id+"FMRX2liYoJm4zaX_1.3.F3.boolean.opBoolean","SPLIT",EDGE,{"disambiguationData":[TD([subQ6])],"derivedFrom":makeQuery(id+"FMRX2liYoJm4zaX_1.2.F3.boolean.opBoolean","SPLIT",EDGE,{"disambiguationData":[TD([subQ6])],"derivedFrom":makeQuery(id+"FMRX2liYoJm4zaX_1.1.F3.boolean.opBoolean","SPLIT",EDGE,{"disambiguationData":[TD([subQ6])],"derivedFrom":makeQuery(id+"F1.opExtrude","CAP_EDGE",EDGE,{"disambiguationData":[OSD([subQ0])],"isStart":false})})})})})})})})})})});}
            var Q49;
            Q49=makeQuery(id+"FMRX2liYoJm4zaX_1.9.F3.boolean.opBoolean","COPY",EDGE,{"derivedFrom":makeQuery(id+"FMRX2liYoJm4zaX_1.9.F3.opExtrude","SWEPT_EDGE",EDGE,{"disambiguationData":[OSD([sQuery(id+"F0.wireOp",EDGE,"E0"),sQuery(id+"F2.wireOp",EDGE,"E2"),sQuery(id+"F2.wireOp",EDGE,"E11.0")])]})});
            var Q50;
            Q50=makeQuery(id+"FMRX2liYoJm4zaX_1.9.F3.boolean.opBoolean","COPY",EDGE,{"derivedFrom":makeQuery(id+"FMRX2liYoJm4zaX_1.9.F3.opExtrude","CAP_EDGE",EDGE,{"disambiguationData":[OSD([sQuery(id+"F2.wireOp",EDGE,"E2")])],"isStart":true})});
            var Q51;
            Q51=makeQuery(id+"FMRX2liYoJm4zaX_1.9.F3.boolean.opBoolean","COPY",EDGE,{"derivedFrom":makeQuery(id+"FMRX2liYoJm4zaX_1.9.F3.opExtrude","CAP_EDGE",EDGE,{"disambiguationData":[OSD([sQuery(id+"F2.wireOp",EDGE,"E10")])],"isStart":true})});
            var Q52;
            Q52=makeQuery(id+"FMRX2liYoJm4zaX_1.9.F3.boolean.opBoolean","COPY",EDGE,{"derivedFrom":makeQuery(id+"FMRX2liYoJm4zaX_1.9.F3.opExtrude","CAP_EDGE",EDGE,{"disambiguationData":[OSD([sQuery(id+"F2.wireOp",EDGE,"E3")])],"isStart":true})});
            var Q53;
            Q53=makeQuery(id+"FMRX2liYoJm4zaX_1.9.F3.boolean.opBoolean","COPY",EDGE,{"derivedFrom":makeQuery(id+"FMRX2liYoJm4zaX_1.9.F3.opExtrude","SWEPT_EDGE",EDGE,{"disambiguationData":[OSD([sQuery(id+"F0.wireOp",EDGE,"E0"),sQuery(id+"F2.wireOp",EDGE,"E3"),sQuery(id+"F2.wireOp",EDGE,"E11.0")])]})});
            var Q54;
            {var subQ0=sQuery(id+"F0.wireOp",EDGE,"E0");var subQ2=sQuery(id+"F2.wireOp",EDGE,"E2");var subQ3=makeQuery(id+"FMRX2liYoJm4zaX_1.8.F3.opExtrude","SWEPT_FACE",FACE,{"disambiguationData":[OSD([subQ2])]});var subQ5=sQuery(id+"F2.wireOp",EDGE,"E3");var subQ6=makeQuery(id+"F3.boolean.opBoolean","COPY",FACE,{"derivedFrom":makeQuery(id+"F3.opExtrude","SWEPT_FACE",FACE,{"disambiguationData":[OSD([subQ5])]})});Q54=makeQuery(id+"FMRX2liYoJm4zaX_1.9.F3.boolean.opBoolean","SPLIT",EDGE,{"disambiguationData":[TD([makeQuery(id+"FMRX2liYoJm4zaX_1.8.F3.boolean.opBoolean","COPY",FACE,{"derivedFrom":subQ3})])],"derivedFrom":makeQuery(id+"FMRX2liYoJm4zaX_1.8.F3.boolean.opBoolean","SPLIT",EDGE,{"disambiguationData":[TD([subQ6])],"derivedFrom":makeQuery(id+"FMRX2liYoJm4zaX_1.7.F3.boolean.opBoolean","SPLIT",EDGE,{"disambiguationData":[TD([subQ6])],"derivedFrom":makeQuery(id+"FMRX2liYoJm4zaX_1.6.F3.boolean.opBoolean","SPLIT",EDGE,{"disambiguationData":[TD([subQ6])],"derivedFrom":makeQuery(id+"FMRX2liYoJm4zaX_1.5.F3.boolean.opBoolean","SPLIT",EDGE,{"disambiguationData":[TD([subQ6])],"derivedFrom":makeQuery(id+"FMRX2liYoJm4zaX_1.4.F3.boolean.opBoolean","SPLIT",EDGE,{"disambiguationData":[TD([subQ6])],"derivedFrom":makeQuery(id+"FMRX2liYoJm4zaX_1.3.F3.boolean.opBoolean","SPLIT",EDGE,{"disambiguationData":[TD([subQ6])],"derivedFrom":makeQuery(id+"FMRX2liYoJm4zaX_1.2.F3.boolean.opBoolean","SPLIT",EDGE,{"disambiguationData":[TD([subQ6])],"derivedFrom":makeQuery(id+"FMRX2liYoJm4zaX_1.1.F3.boolean.opBoolean","SPLIT",EDGE,{"disambiguationData":[TD([subQ6])],"derivedFrom":makeQuery(id+"F1.opExtrude","CAP_EDGE",EDGE,{"disambiguationData":[OSD([subQ0])],"isStart":false})})})})})})})})})});}
            var Q55;
            Q55=makeQuery(id+"FMRX2liYoJm4zaX_1.8.F3.boolean.opBoolean","COPY",EDGE,{"derivedFrom":makeQuery(id+"FMRX2liYoJm4zaX_1.8.F3.opExtrude","SWEPT_EDGE",EDGE,{"disambiguationData":[OSD([sQuery(id+"F0.wireOp",EDGE,"E0"),sQuery(id+"F2.wireOp",EDGE,"E2"),sQuery(id+"F2.wireOp",EDGE,"E11.0")])]})});
            var Q56;
            Q56=makeQuery(id+"FMRX2liYoJm4zaX_1.8.F3.boolean.opBoolean","COPY",EDGE,{"derivedFrom":makeQuery(id+"FMRX2liYoJm4zaX_1.8.F3.opExtrude","CAP_EDGE",EDGE,{"disambiguationData":[OSD([sQuery(id+"F2.wireOp",EDGE,"E2")])],"isStart":true})});
            var Q57;
            Q57=makeQuery(id+"FMRX2liYoJm4zaX_1.8.F3.boolean.opBoolean","COPY",EDGE,{"derivedFrom":makeQuery(id+"FMRX2liYoJm4zaX_1.8.F3.opExtrude","CAP_EDGE",EDGE,{"disambiguationData":[OSD([sQuery(id+"F2.wireOp",EDGE,"E10")])],"isStart":true})});
            var Q58;
            Q58=makeQuery(id+"FMRX2liYoJm4zaX_1.8.F3.boolean.opBoolean","COPY",EDGE,{"derivedFrom":makeQuery(id+"FMRX2liYoJm4zaX_1.8.F3.opExtrude","CAP_EDGE",EDGE,{"disambiguationData":[OSD([sQuery(id+"F2.wireOp",EDGE,"E3")])],"isStart":true})});
            var Q59;
            Q59=makeQuery(id+"FMRX2liYoJm4zaX_1.8.F3.boolean.opBoolean","COPY",EDGE,{"derivedFrom":makeQuery(id+"FMRX2liYoJm4zaX_1.8.F3.opExtrude","SWEPT_EDGE",EDGE,{"disambiguationData":[OSD([sQuery(id+"F0.wireOp",EDGE,"E0"),sQuery(id+"F2.wireOp",EDGE,"E3"),sQuery(id+"F2.wireOp",EDGE,"E11.0")])]})});
            var Q60;
            Q60=makeQuery(id+"FMRX2liYoJm4zaX_1.7.F3.boolean.opBoolean","COPY",EDGE,{"derivedFrom":makeQuery(id+"FMRX2liYoJm4zaX_1.7.F3.opExtrude","SWEPT_EDGE",EDGE,{"disambiguationData":[OSD([sQuery(id+"F0.wireOp",EDGE,"E0"),sQuery(id+"F2.wireOp",EDGE,"E2"),sQuery(id+"F2.wireOp",EDGE,"E11.0")])]})});
            var Q61;
            {var subQ0=sQuery(id+"F0.wireOp",EDGE,"E0");var subQ2=sQuery(id+"F2.wireOp",EDGE,"E2");var subQ3=makeQuery(id+"FMRX2liYoJm4zaX_1.7.F3.opExtrude","SWEPT_FACE",FACE,{"disambiguationData":[OSD([subQ2])]});var subQ4=sQuery(id+"F2.wireOp",EDGE,"E3");var subQ6=makeQuery(id+"F3.boolean.opBoolean","COPY",FACE,{"derivedFrom":makeQuery(id+"F3.opExtrude","SWEPT_FACE",FACE,{"disambiguationData":[OSD([subQ4])]})});Q61=makeQuery(id+"FMRX2liYoJm4zaX_1.8.F3.boolean.opBoolean","SPLIT",EDGE,{"disambiguationData":[TD([makeQuery(id+"FMRX2liYoJm4zaX_1.7.F3.boolean.opBoolean","COPY",FACE,{"derivedFrom":subQ3})])],"derivedFrom":makeQuery(id+"FMRX2liYoJm4zaX_1.7.F3.boolean.opBoolean","SPLIT",EDGE,{"disambiguationData":[TD([subQ6])],"derivedFrom":makeQuery(id+"FMRX2liYoJm4zaX_1.6.F3.boolean.opBoolean","SPLIT",EDGE,{"disambiguationData":[TD([subQ6])],"derivedFrom":makeQuery(id+"FMRX2liYoJm4zaX_1.5.F3.boolean.opBoolean","SPLIT",EDGE,{"disambiguationData":[TD([subQ6])],"derivedFrom":makeQuery(id+"FMRX2liYoJm4zaX_1.4.F3.boolean.opBoolean","SPLIT",EDGE,{"disambiguationData":[TD([subQ6])],"derivedFrom":makeQuery(id+"FMRX2liYoJm4zaX_1.3.F3.boolean.opBoolean","SPLIT",EDGE,{"disambiguationData":[TD([subQ6])],"derivedFrom":makeQuery(id+"FMRX2liYoJm4zaX_1.2.F3.boolean.opBoolean","SPLIT",EDGE,{"disambiguationData":[TD([subQ6])],"derivedFrom":makeQuery(id+"FMRX2liYoJm4zaX_1.1.F3.boolean.opBoolean","SPLIT",EDGE,{"disambiguationData":[TD([subQ6])],"derivedFrom":makeQuery(id+"F1.opExtrude","CAP_EDGE",EDGE,{"disambiguationData":[OSD([subQ0])],"isStart":false})})})})})})})})});}
            var Q62;
            Q62=makeQuery(id+"FMRX2liYoJm4zaX_1.7.F3.boolean.opBoolean","COPY",EDGE,{"derivedFrom":makeQuery(id+"FMRX2liYoJm4zaX_1.7.F3.opExtrude","CAP_EDGE",EDGE,{"disambiguationData":[OSD([sQuery(id+"F2.wireOp",EDGE,"E10")])],"isStart":true})});
            var Q63;
            Q63=makeQuery(id+"FMRX2liYoJm4zaX_1.7.F3.boolean.opBoolean","COPY",EDGE,{"derivedFrom":makeQuery(id+"FMRX2liYoJm4zaX_1.7.F3.opExtrude","CAP_EDGE",EDGE,{"disambiguationData":[OSD([sQuery(id+"F2.wireOp",EDGE,"E2")])],"isStart":true})});
            var Q64;
            Q64=makeQuery(id+"FMRX2liYoJm4zaX_1.7.F3.boolean.opBoolean","COPY",EDGE,{"derivedFrom":makeQuery(id+"FMRX2liYoJm4zaX_1.7.F3.opExtrude","SWEPT_EDGE",EDGE,{"disambiguationData":[OSD([sQuery(id+"F0.wireOp",EDGE,"E0"),sQuery(id+"F2.wireOp",EDGE,"E3"),sQuery(id+"F2.wireOp",EDGE,"E11.0")])]})});
            var Q65;
            Q65=makeQuery(id+"FMRX2liYoJm4zaX_1.7.F3.boolean.opBoolean","COPY",EDGE,{"derivedFrom":makeQuery(id+"FMRX2liYoJm4zaX_1.7.F3.opExtrude","CAP_EDGE",EDGE,{"disambiguationData":[OSD([sQuery(id+"F2.wireOp",EDGE,"E3")])],"isStart":true})});
            var Q66;
            {var subQ0=sQuery(id+"F0.wireOp",EDGE,"E0");var subQ3=sQuery(id+"F2.wireOp",EDGE,"E2");var subQ4=makeQuery(id+"FMRX2liYoJm4zaX_1.6.F3.opExtrude","SWEPT_FACE",FACE,{"disambiguationData":[OSD([subQ3])]});var subQ5=sQuery(id+"F2.wireOp",EDGE,"E3");var subQ6=makeQuery(id+"F3.boolean.opBoolean","COPY",FACE,{"derivedFrom":makeQuery(id+"F3.opExtrude","SWEPT_FACE",FACE,{"disambiguationData":[OSD([subQ5])]})});Q66=makeQuery(id+"FMRX2liYoJm4zaX_1.7.F3.boolean.opBoolean","SPLIT",EDGE,{"disambiguationData":[TD([makeQuery(id+"FMRX2liYoJm4zaX_1.6.F3.boolean.opBoolean","COPY",FACE,{"derivedFrom":subQ4})])],"derivedFrom":makeQuery(id+"FMRX2liYoJm4zaX_1.6.F3.boolean.opBoolean","SPLIT",EDGE,{"disambiguationData":[TD([subQ6])],"derivedFrom":makeQuery(id+"FMRX2liYoJm4zaX_1.5.F3.boolean.opBoolean","SPLIT",EDGE,{"disambiguationData":[TD([subQ6])],"derivedFrom":makeQuery(id+"FMRX2liYoJm4zaX_1.4.F3.boolean.opBoolean","SPLIT",EDGE,{"disambiguationData":[TD([subQ6])],"derivedFrom":makeQuery(id+"FMRX2liYoJm4zaX_1.3.F3.boolean.opBoolean","SPLIT",EDGE,{"disambiguationData":[TD([subQ6])],"derivedFrom":makeQuery(id+"FMRX2liYoJm4zaX_1.2.F3.boolean.opBoolean","SPLIT",EDGE,{"disambiguationData":[TD([subQ6])],"derivedFrom":makeQuery(id+"FMRX2liYoJm4zaX_1.1.F3.boolean.opBoolean","SPLIT",EDGE,{"disambiguationData":[TD([subQ6])],"derivedFrom":makeQuery(id+"F1.opExtrude","CAP_EDGE",EDGE,{"disambiguationData":[OSD([subQ0])],"isStart":false})})})})})})})});}
            var Q67;
            Q67=makeQuery(id+"FMRX2liYoJm4zaX_1.6.F3.boolean.opBoolean","COPY",EDGE,{"derivedFrom":makeQuery(id+"FMRX2liYoJm4zaX_1.6.F3.opExtrude","SWEPT_EDGE",EDGE,{"disambiguationData":[OSD([sQuery(id+"F0.wireOp",EDGE,"E0"),sQuery(id+"F2.wireOp",EDGE,"E2"),sQuery(id+"F2.wireOp",EDGE,"E11.0")])]})});
            var Q68;
            Q68=makeQuery(id+"FMRX2liYoJm4zaX_1.6.F3.boolean.opBoolean","COPY",EDGE,{"derivedFrom":makeQuery(id+"FMRX2liYoJm4zaX_1.6.F3.opExtrude","CAP_EDGE",EDGE,{"disambiguationData":[OSD([sQuery(id+"F2.wireOp",EDGE,"E2")])],"isStart":true})});
            var Q69;
            Q69=makeQuery(id+"FMRX2liYoJm4zaX_1.6.F3.boolean.opBoolean","COPY",EDGE,{"derivedFrom":makeQuery(id+"FMRX2liYoJm4zaX_1.6.F3.opExtrude","CAP_EDGE",EDGE,{"disambiguationData":[OSD([sQuery(id+"F2.wireOp",EDGE,"E10")])],"isStart":true})});
            var Q70;
            Q70=makeQuery(id+"FMRX2liYoJm4zaX_1.6.F3.boolean.opBoolean","COPY",EDGE,{"derivedFrom":makeQuery(id+"FMRX2liYoJm4zaX_1.6.F3.opExtrude","CAP_EDGE",EDGE,{"disambiguationData":[OSD([sQuery(id+"F2.wireOp",EDGE,"E3")])],"isStart":true})});
            var Q71;
            Q71=makeQuery(id+"FMRX2liYoJm4zaX_1.6.F3.boolean.opBoolean","COPY",EDGE,{"derivedFrom":makeQuery(id+"FMRX2liYoJm4zaX_1.6.F3.opExtrude","SWEPT_EDGE",EDGE,{"disambiguationData":[OSD([sQuery(id+"F0.wireOp",EDGE,"E0"),sQuery(id+"F2.wireOp",EDGE,"E3"),sQuery(id+"F2.wireOp",EDGE,"E11.0")])]})});
            var Q72;
            {var subQ0=sQuery(id+"F0.wireOp",EDGE,"E0");var subQ3=sQuery(id+"F2.wireOp",EDGE,"E3");var subQ4=sQuery(id+"F2.wireOp",EDGE,"E2");var subQ5=makeQuery(id+"FMRX2liYoJm4zaX_1.5.F3.opExtrude","SWEPT_FACE",FACE,{"disambiguationData":[OSD([subQ4])]});var subQ6=makeQuery(id+"F3.boolean.opBoolean","COPY",FACE,{"derivedFrom":makeQuery(id+"F3.opExtrude","SWEPT_FACE",FACE,{"disambiguationData":[OSD([subQ3])]})});Q72=makeQuery(id+"FMRX2liYoJm4zaX_1.6.F3.boolean.opBoolean","SPLIT",EDGE,{"disambiguationData":[TD([makeQuery(id+"FMRX2liYoJm4zaX_1.5.F3.boolean.opBoolean","COPY",FACE,{"derivedFrom":subQ5})])],"derivedFrom":makeQuery(id+"FMRX2liYoJm4zaX_1.5.F3.boolean.opBoolean","SPLIT",EDGE,{"disambiguationData":[TD([subQ6])],"derivedFrom":makeQuery(id+"FMRX2liYoJm4zaX_1.4.F3.boolean.opBoolean","SPLIT",EDGE,{"disambiguationData":[TD([subQ6])],"derivedFrom":makeQuery(id+"FMRX2liYoJm4zaX_1.3.F3.boolean.opBoolean","SPLIT",EDGE,{"disambiguationData":[TD([subQ6])],"derivedFrom":makeQuery(id+"FMRX2liYoJm4zaX_1.2.F3.boolean.opBoolean","SPLIT",EDGE,{"disambiguationData":[TD([subQ6])],"derivedFrom":makeQuery(id+"FMRX2liYoJm4zaX_1.1.F3.boolean.opBoolean","SPLIT",EDGE,{"disambiguationData":[TD([subQ6])],"derivedFrom":makeQuery(id+"F1.opExtrude","CAP_EDGE",EDGE,{"disambiguationData":[OSD([subQ0])],"isStart":false})})})})})})});}
            var Q73;
            Q73=makeQuery(id+"FMRX2liYoJm4zaX_1.5.F3.boolean.opBoolean","COPY",EDGE,{"derivedFrom":makeQuery(id+"FMRX2liYoJm4zaX_1.5.F3.opExtrude","SWEPT_EDGE",EDGE,{"disambiguationData":[OSD([sQuery(id+"F0.wireOp",EDGE,"E0"),sQuery(id+"F2.wireOp",EDGE,"E2"),sQuery(id+"F2.wireOp",EDGE,"E11.0")])]})});
            var Q74;
            Q74=makeQuery(id+"FMRX2liYoJm4zaX_1.5.F3.boolean.opBoolean","COPY",EDGE,{"derivedFrom":makeQuery(id+"FMRX2liYoJm4zaX_1.5.F3.opExtrude","CAP_EDGE",EDGE,{"disambiguationData":[OSD([sQuery(id+"F2.wireOp",EDGE,"E2")])],"isStart":true})});
            var Q75;
            Q75=makeQuery(id+"FMRX2liYoJm4zaX_1.5.F3.boolean.opBoolean","COPY",EDGE,{"derivedFrom":makeQuery(id+"FMRX2liYoJm4zaX_1.5.F3.opExtrude","CAP_EDGE",EDGE,{"disambiguationData":[OSD([sQuery(id+"F2.wireOp",EDGE,"E10")])],"isStart":true})});
            var Q76;
            Q76=makeQuery(id+"FMRX2liYoJm4zaX_1.5.F3.boolean.opBoolean","COPY",EDGE,{"derivedFrom":makeQuery(id+"FMRX2liYoJm4zaX_1.5.F3.opExtrude","CAP_EDGE",EDGE,{"disambiguationData":[OSD([sQuery(id+"F2.wireOp",EDGE,"E3")])],"isStart":true})});
            var Q77;
            Q77=makeQuery(id+"FMRX2liYoJm4zaX_1.5.F3.boolean.opBoolean","COPY",EDGE,{"derivedFrom":makeQuery(id+"FMRX2liYoJm4zaX_1.5.F3.opExtrude","SWEPT_EDGE",EDGE,{"disambiguationData":[OSD([sQuery(id+"F0.wireOp",EDGE,"E0"),sQuery(id+"F2.wireOp",EDGE,"E3"),sQuery(id+"F2.wireOp",EDGE,"E11.0")])]})});
            var Q78;
            {var subQ0=sQuery(id+"F0.wireOp",EDGE,"E0");var subQ3=sQuery(id+"F2.wireOp",EDGE,"E2");var subQ4=makeQuery(id+"FMRX2liYoJm4zaX_1.4.F3.opExtrude","SWEPT_FACE",FACE,{"disambiguationData":[OSD([subQ3])]});var subQ5=sQuery(id+"F2.wireOp",EDGE,"E3");var subQ6=makeQuery(id+"F3.boolean.opBoolean","COPY",FACE,{"derivedFrom":makeQuery(id+"F3.opExtrude","SWEPT_FACE",FACE,{"disambiguationData":[OSD([subQ5])]})});Q78=makeQuery(id+"FMRX2liYoJm4zaX_1.5.F3.boolean.opBoolean","SPLIT",EDGE,{"disambiguationData":[TD([makeQuery(id+"FMRX2liYoJm4zaX_1.4.F3.boolean.opBoolean","COPY",FACE,{"derivedFrom":subQ4})])],"derivedFrom":makeQuery(id+"FMRX2liYoJm4zaX_1.4.F3.boolean.opBoolean","SPLIT",EDGE,{"disambiguationData":[TD([subQ6])],"derivedFrom":makeQuery(id+"FMRX2liYoJm4zaX_1.3.F3.boolean.opBoolean","SPLIT",EDGE,{"disambiguationData":[TD([subQ6])],"derivedFrom":makeQuery(id+"FMRX2liYoJm4zaX_1.2.F3.boolean.opBoolean","SPLIT",EDGE,{"disambiguationData":[TD([subQ6])],"derivedFrom":makeQuery(id+"FMRX2liYoJm4zaX_1.1.F3.boolean.opBoolean","SPLIT",EDGE,{"disambiguationData":[TD([subQ6])],"derivedFrom":makeQuery(id+"F1.opExtrude","CAP_EDGE",EDGE,{"disambiguationData":[OSD([subQ0])],"isStart":false})})})})})});}
            var Q79;
            Q79=makeQuery(id+"FMRX2liYoJm4zaX_1.4.F3.boolean.opBoolean","COPY",EDGE,{"derivedFrom":makeQuery(id+"FMRX2liYoJm4zaX_1.4.F3.opExtrude","CAP_EDGE",EDGE,{"disambiguationData":[OSD([sQuery(id+"F2.wireOp",EDGE,"E2")])],"isStart":true})});
            var Q80;
            Q80=makeQuery(id+"FMRX2liYoJm4zaX_1.4.F3.boolean.opBoolean","COPY",EDGE,{"derivedFrom":makeQuery(id+"FMRX2liYoJm4zaX_1.4.F3.opExtrude","CAP_EDGE",EDGE,{"disambiguationData":[OSD([sQuery(id+"F2.wireOp",EDGE,"E10")])],"isStart":true})});
            var Q81;
            Q81=makeQuery(id+"FMRX2liYoJm4zaX_1.4.F3.boolean.opBoolean","COPY",EDGE,{"derivedFrom":makeQuery(id+"FMRX2liYoJm4zaX_1.4.F3.opExtrude","CAP_EDGE",EDGE,{"disambiguationData":[OSD([sQuery(id+"F2.wireOp",EDGE,"E3")])],"isStart":true})});
            var Q82;
            Q82=makeQuery(id+"FMRX2liYoJm4zaX_1.4.F3.boolean.opBoolean","COPY",EDGE,{"derivedFrom":makeQuery(id+"FMRX2liYoJm4zaX_1.4.F3.opExtrude","SWEPT_EDGE",EDGE,{"disambiguationData":[OSD([sQuery(id+"F0.wireOp",EDGE,"E0"),sQuery(id+"F2.wireOp",EDGE,"E3"),sQuery(id+"F2.wireOp",EDGE,"E11.0")])]})});
            var Q83;
            {var subQ0=sQuery(id+"F0.wireOp",EDGE,"E0");var subQ2=sQuery(id+"F2.wireOp",EDGE,"E3");var subQ4=sQuery(id+"F2.wireOp",EDGE,"E2");var subQ5=makeQuery(id+"FMRX2liYoJm4zaX_1.3.F3.opExtrude","SWEPT_FACE",FACE,{"disambiguationData":[OSD([subQ4])]});var subQ6=makeQuery(id+"F3.boolean.opBoolean","COPY",FACE,{"derivedFrom":makeQuery(id+"F3.opExtrude","SWEPT_FACE",FACE,{"disambiguationData":[OSD([subQ2])]})});Q83=makeQuery(id+"FMRX2liYoJm4zaX_1.4.F3.boolean.opBoolean","SPLIT",EDGE,{"disambiguationData":[TD([makeQuery(id+"FMRX2liYoJm4zaX_1.3.F3.boolean.opBoolean","COPY",FACE,{"derivedFrom":subQ5})])],"derivedFrom":makeQuery(id+"FMRX2liYoJm4zaX_1.3.F3.boolean.opBoolean","SPLIT",EDGE,{"disambiguationData":[TD([subQ6])],"derivedFrom":makeQuery(id+"FMRX2liYoJm4zaX_1.2.F3.boolean.opBoolean","SPLIT",EDGE,{"disambiguationData":[TD([subQ6])],"derivedFrom":makeQuery(id+"FMRX2liYoJm4zaX_1.1.F3.boolean.opBoolean","SPLIT",EDGE,{"disambiguationData":[TD([subQ6])],"derivedFrom":makeQuery(id+"F1.opExtrude","CAP_EDGE",EDGE,{"disambiguationData":[OSD([subQ0])],"isStart":false})})})})});}
            var Q84;
            Q84=makeQuery(id+"FMRX2liYoJm4zaX_1.4.F3.boolean.opBoolean","COPY",EDGE,{"derivedFrom":makeQuery(id+"FMRX2liYoJm4zaX_1.4.F3.opExtrude","SWEPT_EDGE",EDGE,{"disambiguationData":[OSD([sQuery(id+"F0.wireOp",EDGE,"E0"),sQuery(id+"F2.wireOp",EDGE,"E2"),sQuery(id+"F2.wireOp",EDGE,"E11.0")])]})});
            var Q85;
            Q85=makeQuery(id+"FMRX2liYoJm4zaX_1.3.F3.boolean.opBoolean","COPY",EDGE,{"derivedFrom":makeQuery(id+"FMRX2liYoJm4zaX_1.3.F3.opExtrude","SWEPT_EDGE",EDGE,{"disambiguationData":[OSD([sQuery(id+"F0.wireOp",EDGE,"E0"),sQuery(id+"F2.wireOp",EDGE,"E2"),sQuery(id+"F2.wireOp",EDGE,"E11.0")])]})});
            var Q86;
            Q86=makeQuery(id+"FMRX2liYoJm4zaX_1.3.F3.boolean.opBoolean","COPY",EDGE,{"derivedFrom":makeQuery(id+"FMRX2liYoJm4zaX_1.3.F3.opExtrude","CAP_EDGE",EDGE,{"disambiguationData":[OSD([sQuery(id+"F2.wireOp",EDGE,"E2")])],"isStart":true})});
            var Q87;
            Q87=makeQuery(id+"FMRX2liYoJm4zaX_1.3.F3.boolean.opBoolean","COPY",EDGE,{"derivedFrom":makeQuery(id+"FMRX2liYoJm4zaX_1.3.F3.opExtrude","CAP_EDGE",EDGE,{"disambiguationData":[OSD([sQuery(id+"F2.wireOp",EDGE,"E10")])],"isStart":true})});
            var Q88;
            Q88=makeQuery(id+"FMRX2liYoJm4zaX_1.3.F3.boolean.opBoolean","COPY",EDGE,{"derivedFrom":makeQuery(id+"FMRX2liYoJm4zaX_1.3.F3.opExtrude","CAP_EDGE",EDGE,{"disambiguationData":[OSD([sQuery(id+"F2.wireOp",EDGE,"E3")])],"isStart":true})});
            var Q89;
            Q89=makeQuery(id+"FMRX2liYoJm4zaX_1.3.F3.boolean.opBoolean","COPY",EDGE,{"derivedFrom":makeQuery(id+"FMRX2liYoJm4zaX_1.3.F3.opExtrude","SWEPT_EDGE",EDGE,{"disambiguationData":[OSD([sQuery(id+"F0.wireOp",EDGE,"E0"),sQuery(id+"F2.wireOp",EDGE,"E3"),sQuery(id+"F2.wireOp",EDGE,"E11.0")])]})});
            var Q90;
            {var subQ0=sQuery(id+"F0.wireOp",EDGE,"E0");var subQ3=sQuery(id+"F2.wireOp",EDGE,"E2");var subQ4=makeQuery(id+"FMRX2liYoJm4zaX_1.2.F3.opExtrude","SWEPT_FACE",FACE,{"disambiguationData":[OSD([subQ3])]});var subQ5=sQuery(id+"F2.wireOp",EDGE,"E3");var subQ6=makeQuery(id+"F3.boolean.opBoolean","COPY",FACE,{"derivedFrom":makeQuery(id+"F3.opExtrude","SWEPT_FACE",FACE,{"disambiguationData":[OSD([subQ5])]})});Q90=makeQuery(id+"FMRX2liYoJm4zaX_1.3.F3.boolean.opBoolean","SPLIT",EDGE,{"disambiguationData":[TD([makeQuery(id+"FMRX2liYoJm4zaX_1.2.F3.boolean.opBoolean","COPY",FACE,{"derivedFrom":subQ4})])],"derivedFrom":makeQuery(id+"FMRX2liYoJm4zaX_1.2.F3.boolean.opBoolean","SPLIT",EDGE,{"disambiguationData":[TD([subQ6])],"derivedFrom":makeQuery(id+"FMRX2liYoJm4zaX_1.1.F3.boolean.opBoolean","SPLIT",EDGE,{"disambiguationData":[TD([subQ6])],"derivedFrom":makeQuery(id+"F1.opExtrude","CAP_EDGE",EDGE,{"disambiguationData":[OSD([subQ0])],"isStart":false})})})});}
            var Q91;
            Q91=makeQuery(id+"FMRX2liYoJm4zaX_1.2.F3.boolean.opBoolean","COPY",EDGE,{"derivedFrom":makeQuery(id+"FMRX2liYoJm4zaX_1.2.F3.opExtrude","SWEPT_EDGE",EDGE,{"disambiguationData":[OSD([sQuery(id+"F0.wireOp",EDGE,"E0"),sQuery(id+"F2.wireOp",EDGE,"E2"),sQuery(id+"F2.wireOp",EDGE,"E11.0")])]})});
            var Q92;
            Q92=makeQuery(id+"FMRX2liYoJm4zaX_1.2.F3.boolean.opBoolean","COPY",EDGE,{"derivedFrom":makeQuery(id+"FMRX2liYoJm4zaX_1.2.F3.opExtrude","CAP_EDGE",EDGE,{"disambiguationData":[OSD([sQuery(id+"F2.wireOp",EDGE,"E2")])],"isStart":true})});
            var Q93;
            Q93=makeQuery(id+"FMRX2liYoJm4zaX_1.2.F3.boolean.opBoolean","COPY",EDGE,{"derivedFrom":makeQuery(id+"FMRX2liYoJm4zaX_1.2.F3.opExtrude","CAP_EDGE",EDGE,{"disambiguationData":[OSD([sQuery(id+"F2.wireOp",EDGE,"E10")])],"isStart":true})});
            var Q94;
            Q94=makeQuery(id+"FMRX2liYoJm4zaX_1.2.F3.boolean.opBoolean","COPY",EDGE,{"derivedFrom":makeQuery(id+"FMRX2liYoJm4zaX_1.2.F3.opExtrude","SWEPT_EDGE",EDGE,{"disambiguationData":[OSD([sQuery(id+"F0.wireOp",EDGE,"E0"),sQuery(id+"F2.wireOp",EDGE,"E3"),sQuery(id+"F2.wireOp",EDGE,"E11.0")])]})});
            var Q95;
            Q95=makeQuery(id+"FMRX2liYoJm4zaX_1.1.F3.boolean.opBoolean","COPY",EDGE,{"derivedFrom":makeQuery(id+"FMRX2liYoJm4zaX_1.1.F3.opExtrude","SWEPT_EDGE",EDGE,{"disambiguationData":[OSD([sQuery(id+"F0.wireOp",EDGE,"E0"),sQuery(id+"F2.wireOp",EDGE,"E2"),sQuery(id+"F2.wireOp",EDGE,"E11.0")])]})});
            var Q96;
            {var subQ0=sQuery(id+"F0.wireOp",EDGE,"E0");var subQ3=sQuery(id+"F2.wireOp",EDGE,"E3");var subQ4=makeQuery(id+"FMRX2liYoJm4zaX_1.1.F3.opExtrude","SWEPT_FACE",FACE,{"disambiguationData":[OSD([sQuery(id+"F2.wireOp",EDGE,"E2")])]});Q96=makeQuery(id+"FMRX2liYoJm4zaX_1.2.F3.boolean.opBoolean","SPLIT",EDGE,{"disambiguationData":[TD([makeQuery(id+"FMRX2liYoJm4zaX_1.1.F3.boolean.opBoolean","COPY",FACE,{"derivedFrom":subQ4})])],"derivedFrom":makeQuery(id+"FMRX2liYoJm4zaX_1.1.F3.boolean.opBoolean","SPLIT",EDGE,{"disambiguationData":[TD([makeQuery(id+"F3.boolean.opBoolean","COPY",FACE,{"derivedFrom":makeQuery(id+"F3.opExtrude","SWEPT_FACE",FACE,{"disambiguationData":[OSD([subQ3])]})})])],"derivedFrom":makeQuery(id+"F1.opExtrude","CAP_EDGE",EDGE,{"disambiguationData":[OSD([subQ0])],"isStart":false})})});}
            var Q97;
            Q97=makeQuery(id+"FMRX2liYoJm4zaX_1.2.F3.boolean.opBoolean","COPY",EDGE,{"derivedFrom":makeQuery(id+"FMRX2liYoJm4zaX_1.2.F3.opExtrude","CAP_EDGE",EDGE,{"disambiguationData":[OSD([sQuery(id+"F2.wireOp",EDGE,"E3")])],"isStart":true})});
            var Q98;
            Q98=makeQuery(id+"FMRX2liYoJm4zaX_1.1.F3.boolean.opBoolean","COPY",EDGE,{"derivedFrom":makeQuery(id+"FMRX2liYoJm4zaX_1.1.F3.opExtrude","CAP_EDGE",EDGE,{"disambiguationData":[OSD([sQuery(id+"F2.wireOp",EDGE,"E2")])],"isStart":true})});
            var Q99;
            Q99=makeQuery(id+"FMRX2liYoJm4zaX_1.1.F3.boolean.opBoolean","COPY",EDGE,{"derivedFrom":makeQuery(id+"FMRX2liYoJm4zaX_1.1.F3.opExtrude","CAP_EDGE",EDGE,{"disambiguationData":[OSD([sQuery(id+"F2.wireOp",EDGE,"E10")])],"isStart":true})});
            var Q100;
            Q100=makeQuery(id+"FMRX2liYoJm4zaX_1.1.F3.boolean.opBoolean","COPY",EDGE,{"derivedFrom":makeQuery(id+"FMRX2liYoJm4zaX_1.1.F3.opExtrude","CAP_EDGE",EDGE,{"disambiguationData":[OSD([sQuery(id+"F2.wireOp",EDGE,"E3")])],"isStart":true})});
            var Q101;
            Q101=makeQuery(id+"FMRX2liYoJm4zaX_1.1.F3.boolean.opBoolean","COPY",EDGE,{"derivedFrom":makeQuery(id+"FMRX2liYoJm4zaX_1.1.F3.opExtrude","SWEPT_EDGE",EDGE,{"disambiguationData":[OSD([sQuery(id+"F0.wireOp",EDGE,"E0"),sQuery(id+"F2.wireOp",EDGE,"E3"),sQuery(id+"F2.wireOp",EDGE,"E11.0")])]})});
            var Q102;
            {var subQ0=sQuery(id+"F0.wireOp",EDGE,"E0");Q102=makeQuery(id+"FMRX2liYoJm4zaX_1.1.F3.boolean.opBoolean","SPLIT",EDGE,{"disambiguationData":[TD([makeQuery(id+"F3.boolean.opBoolean","COPY",FACE,{"derivedFrom":makeQuery(id+"F3.opExtrude","SWEPT_FACE",FACE,{"disambiguationData":[OSD([sQuery(id+"F2.wireOp",EDGE,"E2")])]})})])],"derivedFrom":makeQuery(id+"F1.opExtrude","CAP_EDGE",EDGE,{"disambiguationData":[OSD([subQ0])],"isStart":false})});}
            var Q103;
            Q103=makeQuery(id+"F3.boolean.opBoolean","COPY",EDGE,{"derivedFrom":makeQuery(id+"F3.opExtrude","CAP_EDGE",EDGE,{"disambiguationData":[OSD([sQuery(id+"F2.wireOp",EDGE,"E2")])],"isStart":true})});
            var Q104;
            Q104=makeQuery(id+"F3.boolean.opBoolean","COPY",EDGE,{"derivedFrom":makeQuery(id+"F3.opExtrude","SWEPT_EDGE",EDGE,{"disambiguationData":[OSD([sQuery(id+"F0.wireOp",EDGE,"E0"),sQuery(id+"F2.wireOp",EDGE,"E2"),sQuery(id+"F2.wireOp",EDGE,"E11.0")])]})});
            var Q105;
            Q105=makeQuery(id+"F3.boolean.opBoolean","COPY",EDGE,{"derivedFrom":makeQuery(id+"F3.opExtrude","CAP_EDGE",EDGE,{"disambiguationData":[OSD([sQuery(id+"F2.wireOp",EDGE,"E10")])],"isStart":true})});
            var Q106;
            Q106=makeQuery(id+"F3.boolean.opBoolean","COPY",EDGE,{"derivedFrom":makeQuery(id+"F3.opExtrude","CAP_EDGE",EDGE,{"disambiguationData":[OSD([sQuery(id+"F2.wireOp",EDGE,"E3")])],"isStart":true})});
            fillet(context, id + "F7", {"entities" : qUnion([Q0, Q1, Q2, Q3, Q4, Q5, Q6, Q7, Q8, Q9, Q10, Q11, Q12, Q13, Q14, Q15, Q16, Q17, Q18, Q19, Q20, Q21, Q22, Q23, Q24, Q25, Q26, Q27, Q28, Q29, Q30, Q31, Q32, Q33, Q34, Q35, Q36, Q37, Q38, Q39, Q40, Q41, Q42, Q43, Q44, Q45, Q46, Q47, Q48, Q49, Q50, Q51, Q52, Q53, Q54, Q55, Q56, Q57, Q58, Q59, Q60, Q61, Q62, Q63, Q64, Q65, Q66, Q67, Q68, Q69, Q70, Q71, Q72, Q73, Q74, Q75, Q76, Q77, Q78, Q79, Q80, Q81, Q82, Q83, Q84, Q85, Q86, Q87, Q88, Q89, Q90, Q91, Q92, Q93, Q94, Q95, Q96, Q97, Q98, Q99, Q100, Q101, Q102, Q103, Q104, Q105, Q106]), "radius" : 0.2 * mm, "tangentPropagation" : true, "allowEdgeOverflow" : false});
        }
        {
            var Q0;
            Q0=makeQuery(id+"F1.opExtrude","CAP_EDGE",EDGE,{"disambiguationData":[OSD([sQuery(id+"F0.wireOp",EDGE,"E1")])],"isStart":false});
            var Q1;
            Q1=makeQuery(id+"F6.opFillet","BLEND_FACE",FACE,{"disambiguationData":[OSD([sQuery(id+"F0.wireOp",EDGE,"E1")])]});
            fillet(context, id + "F8", {"entities" : qUnion([Q0, Q1]), "radius" : .2 * mm, "tangentPropagation" : true, "allowEdgeOverflow" : false});
        }
    });
